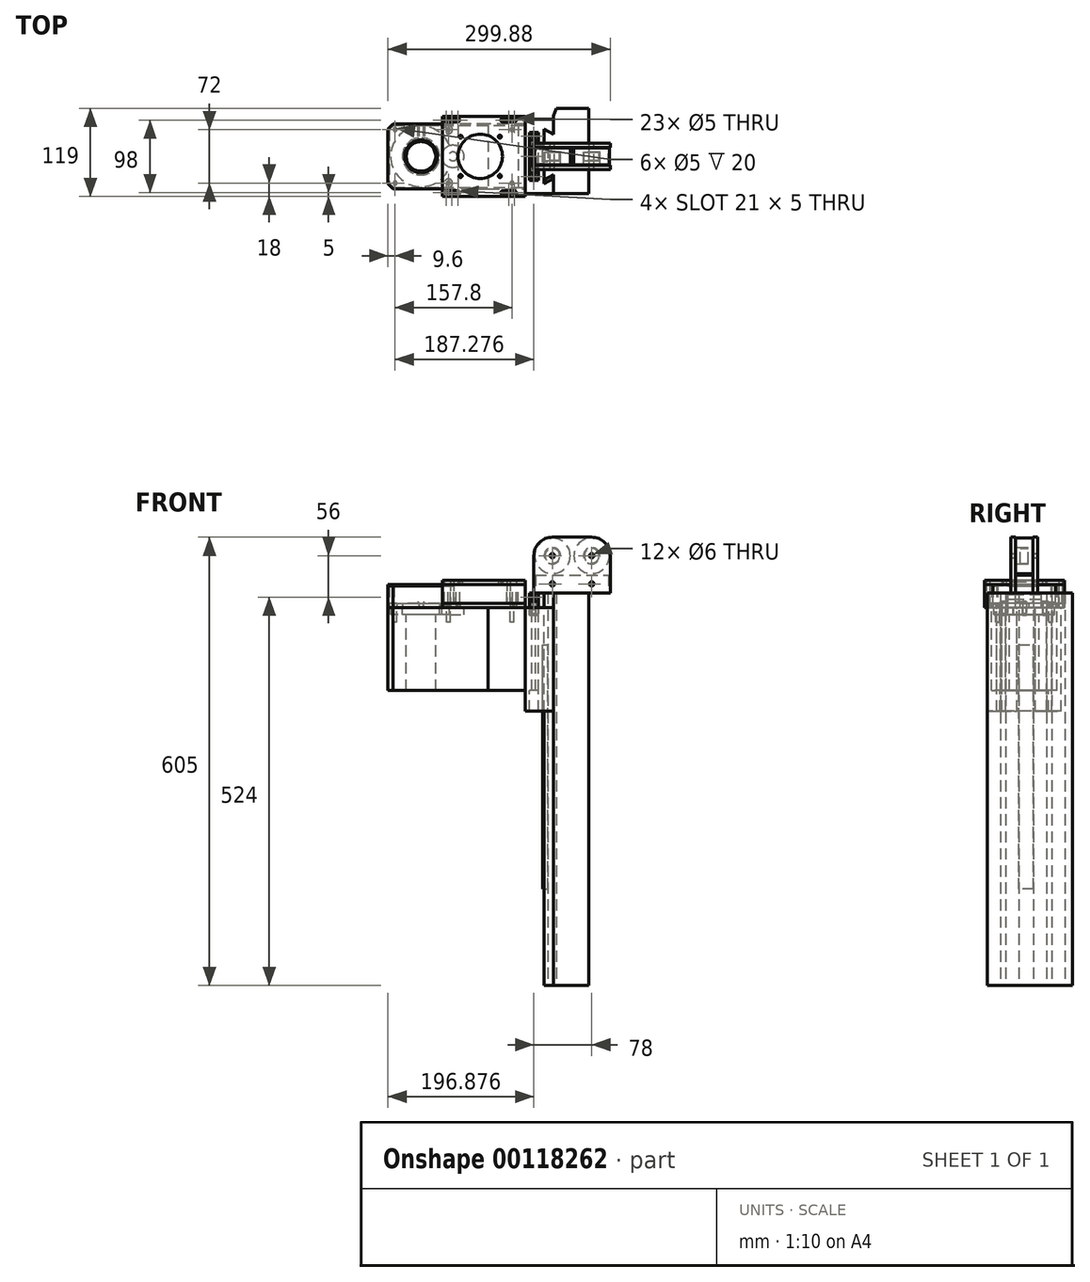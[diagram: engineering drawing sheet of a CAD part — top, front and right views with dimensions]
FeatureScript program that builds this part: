
annotation { "Feature Type Name" : "Feature", "Feature Type Description" : "" }
export const myFeature = defineFeature(function(context is Context, id is Id, definition is map)
    precondition{}
    {
        {
            var Q0;
            Q0=qCreatedBy(makeId("Top.planeOp"),FACE);
            cPlane(context, id + "F0", {"entities" : qUnion([Q0]), "cplaneType" : CPlaneType.OFFSET, "offset" : 31 * mm, "width" : 150 * mm, "height" : 150 * mm});
        }
        {
            var Q0;
            Q0=qCreatedBy(makeId("Top.planeOp"),FACE);
            var sketch = newSketch(context, id + "F1", { "sketchPlane" : qUnion([Q0])});
            skLineSegment(sketch, "E0", {"start": v(0, 0) * mm, "end": v(-38, 0) * mm});
            skLineSegment(sketch, "E1", {"start": v(-38, 0) * mm, "end": v(-38, -6) * mm});
            skLineSegment(sketch, "E2", {"start": v(-38, -6) * mm, "end": v(-88, -6) * mm});
            skLineSegment(sketch, "E3", {"start": v(-88, -6) * mm, "end": v(-88, -94) * mm});
            skLineSegment(sketch, "E4", {"start": v(-88, -94) * mm, "end": v(-38, -94) * mm});
            skLineSegment(sketch, "E5", {"start": v(-38, -94) * mm, "end": v(-38, -100) * mm});
            skLineSegment(sketch, "E6", {"start": v(-38, -100) * mm, "end": v(0, -100) * mm});
            skLineSegment(sketch, "E7", {"start": v(0, -100) * mm, "end": v(0, -80) * mm});
            skLineSegment(sketch, "E8", {"start": v(0, -80) * mm, "end": v(-12.12, -87) * mm});
            skLineSegment(sketch, "E9", {"start": v(-12.12, -87) * mm, "end": v(-12.12, -60) * mm});
            skLineSegment(sketch, "E10", {"start": v(-12.12, -60) * mm, "end": v(-20.12, -60) * mm});
            skLineSegment(sketch, "E11", {"start": v(-20.12, -60) * mm, "end": v(-20.12, -35) * mm});
            skLineSegment(sketch, "E12", {"start": v(-20.12, -35) * mm, "end": v(-12.12, -35) * mm});
            skLineSegment(sketch, "E13", {"start": v(-12.12, -35) * mm, "end": v(-12.12, -13) * mm});
            skLineSegment(sketch, "E14", {"start": v(-12.12, -13) * mm, "end": v(0, -20) * mm});
            skLineSegment(sketch, "E15", {"start": v(0, -20) * mm, "end": v(0, 0) * mm});
            skLineSegment(sketch, "E16", {"start": v(-88, -6) * mm, "end": v(-215.93, -6) * mm});
            skLineSegment(sketch, "E17", {"start": v(-223, -13.07) * mm, "end": v(-223, -86.93) * mm});
            skLineSegment(sketch, "E18", {"start": v(-215.93, -94) * mm, "end": v(-88, -94) * mm});
            skLineSegment(sketch, "E19", {"start": v(-215.93, -6) * mm, "end": v(-223, -13.07) * mm});
            skLineSegment(sketch, "E20", {"start": v(-215.93, -94) * mm, "end": v(-223, -86.93) * mm});
            skCircle(sketch, "E21", {"center": v(-213.4, -86) * mm, "radius": 2.5 * mm});
            skCircle(sketch, "E22.0.1.0", {"center": v(-213.4, -14) * mm, "radius": 2.5 * mm});
            skCircle(sketch, "E22.1.0.0", {"center": v(-141.4, -86) * mm, "radius": 2.5 * mm});
            skCircle(sketch, "E22.1.1.0", {"center": v(-141.4, -14) * mm, "radius": 2.5 * mm});
            skLineSegment(sketch, "E22.direction1", {"start": v(-213.4, -86) * mm, "end": v(-141.4, -86) * mm, "construction": true});
            skLineSegment(sketch, "E22.direction2", {"start": v(-213.4, -86) * mm, "end": v(-213.4, -14) * mm, "construction": true});
            skCircle(sketch, "E23.1.0.0", {"center": v(-55.6, -14) * mm, "radius": 2.5 * mm});
            skCircle(sketch, "E23.1.1.0", {"center": v(-55.6, -86) * mm, "radius": 2.5 * mm});
            skLineSegment(sketch, "E23.direction1", {"start": v(-141.4, -14) * mm, "end": v(-55.6, -14) * mm, "construction": true});
            skLineSegment(sketch, "E23.direction2", {"start": v(-141.4, -14) * mm, "end": v(-141.4, -86) * mm, "construction": true});
            skLineSegment(sketch, "E24", {"start": v(-55.6, -14) * mm, "end": v(-55.6, -86) * mm, "construction": true});
            skLineSegment(sketch, "E25", {"start": v(-55.6, -86) * mm, "end": v(-141.4, -86) * mm, "construction": true});
            skLineSegment(sketch, "E26", {"start": v(-98.5, -14) * mm, "end": v(-98.5, -86) * mm, "construction": true});
            skPoint(sketch, "E27", {"position": v(-98.5, -50) * mm});
            skLineSegment(sketch, "E28", {"start": v(-223, -50) * mm, "end": v(-98.5, -50) * mm, "construction": true});
            skCircle(sketch, "E29", {"center": v(-178.5, -50) * mm, "radius": 25 * mm});
            skCircle(sketch, "E30", {"center": v(-135.42, -50) * mm, "radius": 15 * mm});
            skCircle(sketch, "E31", {"center": v(-178.5, -50) * mm, "radius": 14 * mm});
            skCircle(sketch, "E32", {"center": v(-178.5, -50) * mm, "radius": 20 * mm});
            skCircle(sketch, "E33", {"center": v(-178.5, -50) * mm, "radius": 41 * mm});
            skLineSegment(sketch, "E34", {"start": v(-38, -6) * mm, "end": v(-38, -94) * mm});
            skLineSegment(sketch, "E35", {"start": v(-20.12, -17.5) * mm, "end": v(-32.12, -17.5) * mm});
            skLineSegment(sketch, "E36", {"start": v(-20.12, -17.5) * mm, "end": v(-20.12, -35) * mm});
            skLineSegment(sketch, "E37", {"start": v(-32.12, -17.5) * mm, "end": v(-32.12, -82.5) * mm});
            skLineSegment(sketch, "E38", {"start": v(-32.12, -27.5) * mm, "end": v(-20.12, -27.5) * mm});
            skLineSegment(sketch, "E39.MirrorCS", {"start": v(-32.12, -72.5) * mm, "end": v(-20.12, -72.5) * mm});
            skLineSegment(sketch, "E40.MirrorCS", {"start": v(-20.12, -82.5) * mm, "end": v(-32.12, -82.5) * mm});
            skLineSegment(sketch, "E41", {"start": v(-20.12, -82.5) * mm, "end": v(-20.12, -60) * mm});
            skLineSegment(sketch, "E42", {"start": v(-32.12, -37.5) * mm, "end": v(-20.12, -37.5) * mm});
            skLineSegment(sketch, "E43.MirrorCS", {"start": v(-32.12, -62.5) * mm, "end": v(-20.12, -62.5) * mm});
            skLineSegment(sketch, "E44", {"start": v(-32.12, -27.5) * mm, "end": v(-20.12, -17.5) * mm, "construction": true});
            skLineSegment(sketch, "E45", {"start": v(-20.12, -27.5) * mm, "end": v(-32.12, -17.5) * mm, "construction": true});
            skCircle(sketch, "E46", {"center": v(-26.12, -22.5) * mm, "radius": 2.5 * mm});
            skCircle(sketch, "E47.MirrorC", {"center": v(-26.12, -77.5) * mm, "radius": 2.5 * mm});
            skCircle(sketch, "E48", {"center": v(-26.12, -50) * mm, "radius": 2.5 * mm});
            skPoint(sketch, "E48.centerSnap0", {"position": v(-26.12, -62.5) * mm});
            skPoint(sketch, "E48.centerSnap1", {"position": v(-32.12, -50) * mm});
            skSolve(sketch);
        }
        {
            var Q0;
            Q0=qCreatedBy(makeId("Top.planeOp"),FACE);
            var sketch = newSketch(context, id + "F2", { "sketchPlane" : qUnion([Q0])});
            skLineSegment(sketch, "E49.0", {"start": v(-88, -6) * mm, "end": v(-149.4, -6) * mm});
            skLineSegment(sketch, "E49.4", {"start": v(-149.4, -94) * mm, "end": v(-88, -94) * mm});
            skLineSegment(sketch, "E49.5", {"start": v(-47.6, -6) * mm, "end": v(-88, -6) * mm});
            skLineSegment(sketch, "E49.6", {"start": v(-88, -94) * mm, "end": v(-47.6, -94) * mm});
            skCircle(sketch, "E49.7", {"center": v(-55.6, -86) * mm, "radius": 2.5 * mm});
            skCircle(sketch, "E49.8", {"center": v(-55.6, -14) * mm, "radius": 2.5 * mm});
            skCircle(sketch, "E49.9", {"center": v(-141.4, -14) * mm, "radius": 2.5 * mm});
            skCircle(sketch, "E49.10", {"center": v(-141.4, -86) * mm, "radius": 2.5 * mm});
            skCircle(sketch, "E49.11", {"center": v(-213.4, -86) * mm, "radius": 2.5 * mm});
            skCircle(sketch, "E49.12", {"center": v(-213.4, -14) * mm, "radius": 2.5 * mm});
            skLineSegment(sketch, "E49.13", {"start": v(-98.5, -14) * mm, "end": v(-98.5, -86) * mm, "construction": true});
            skLineSegment(sketch, "E49.14", {"start": v(-141.4, -14) * mm, "end": v(-55.6, -14) * mm, "construction": true});
            skLineSegment(sketch, "E49.15", {"start": v(-55.6, -14) * mm, "end": v(-55.6, -86) * mm, "construction": true});
            skLineSegment(sketch, "E49.16", {"start": v(-55.6, -86) * mm, "end": v(-141.4, -86) * mm, "construction": true});
            skLineSegment(sketch, "E49.17", {"start": v(-141.4, -14) * mm, "end": v(-141.4, -86) * mm, "construction": true});
            skCircle(sketch, "E49.18", {"center": v(-178.5, -50) * mm, "radius": 25 * mm});
            skLineSegment(sketch, "E50", {"start": v(-47.6, -6) * mm, "end": v(-47.6, -94) * mm});
            skLineSegment(sketch, "E51", {"start": v(-149.4, -6) * mm, "end": v(-149.4, -94) * mm, "construction": true});
            skPoint(sketch, "E52", {"position": v(-149.4, -6) * mm});
            skPoint(sketch, "E53", {"position": v(-149.4, -94) * mm});
            skPoint(sketch, "E54.orphan", {"position": v(-215.93, -94) * mm});
            skLineSegment(sketch, "E55.0", {"start": v(-215.1, -8) * mm, "end": v(-149.4, -8) * mm});
            skLineSegment(sketch, "E55.1", {"start": v(-215.1, -92) * mm, "end": v(-149.4, -92) * mm});
            skLineSegment(sketch, "E55.2", {"start": v(-215.1, -92) * mm, "end": v(-221, -86.1) * mm});
            skLineSegment(sketch, "E55.3", {"start": v(-221, -13.9) * mm, "end": v(-221, -86.1) * mm});
            skLineSegment(sketch, "E55.4", {"start": v(-215.1, -8) * mm, "end": v(-221, -13.9) * mm});
            skLineSegment(sketch, "E56.0", {"start": v(-88, 4) * mm, "end": v(-149.4, 4) * mm});
            skLineSegment(sketch, "E56.1", {"start": v(-47.6, 4) * mm, "end": v(-88, 4) * mm});
            skLineSegment(sketch, "E57.0", {"start": v(-88, -104) * mm, "end": v(-47.6, -104) * mm});
            skLineSegment(sketch, "E57.1", {"start": v(-149.4, -104) * mm, "end": v(-88, -104) * mm});
            skLineSegment(sketch, "E58", {"start": v(-149.4, -92) * mm, "end": v(-149.4, -94) * mm});
            skLineSegment(sketch, "E59", {"start": v(-149.4, -104) * mm, "end": v(-149.4, -94) * mm});
            skLineSegment(sketch, "E60", {"start": v(-47.6, -104) * mm, "end": v(-47.6, -94) * mm});
            skLineSegment(sketch, "E61", {"start": v(-149.4, -6) * mm, "end": v(-149.4, 4) * mm});
            skLineSegment(sketch, "E62", {"start": v(-47.6, -6) * mm, "end": v(-47.6, 4) * mm});
            skLineSegment(sketch, "E63", {"start": v(-149.4, -8) * mm, "end": v(-149.4, -6) * mm});
            skPoint(sketch, "E49.2.end.orphan", {"position": v(-223, -86.93) * mm});
            skPoint(sketch, "E49.3.end.orphan", {"position": v(-223, -86.93) * mm});
            skCircle(sketch, "E64", {"center": v(-98.5, -50) * mm, "radius": 25 * mm});
            skLineSegment(sketch, "E65", {"start": v(-178.5, -25) * mm, "end": v(-98.5, -25) * mm});
            skLineSegment(sketch, "E66", {"start": v(-178.5, -75) * mm, "end": v(-98.5, -75) * mm});
            skCircle(sketch, "E67", {"center": v(-98.5, -50) * mm, "radius": 45 * mm, "construction": true});
            skPoint(sketch, "E68.centerSnap0", {"position": v(-149.4, -99) * mm});
            skLineSegment(sketch, "E69", {"start": v(-47.6, 4) * mm, "end": v(-149.4, -104) * mm, "construction": true});
            skLineSegment(sketch, "E70", {"start": v(-149.4, 4) * mm, "end": v(-47.6, -104) * mm, "construction": true});
            skPoint(sketch, "E71.centerSnap0", {"position": v(-47.6, -99) * mm});
            skCircle(sketch, "E72", {"center": v(-144.69, -99) * mm, "radius": 2.5 * mm});
            skCircle(sketch, "E73", {"center": v(-144.69, -1) * mm, "radius": 2.5 * mm});
            skCircle(sketch, "E74", {"center": v(-52.31, -1) * mm, "radius": 2.5 * mm});
            skCircle(sketch, "E75", {"center": v(-52.31, -99) * mm, "radius": 2.5 * mm});
            skCircle(sketch, "E76", {"center": v(-136.69, -1) * mm, "radius": 2.1 * mm});
            skCircle(sketch, "E77", {"center": v(-60.31, -1) * mm, "radius": 2.1 * mm});
            skCircle(sketch, "E78", {"center": v(-136.69, -99) * mm, "radius": 2.1 * mm});
            skCircle(sketch, "E79", {"center": v(-60.31, -99) * mm, "radius": 2.1 * mm});
            skLineSegment(sketch, "E80", {"start": v(-47.6, 4) * mm, "end": v(-38, 4) * mm});
            skLineSegment(sketch, "E81", {"start": v(-38, 4) * mm, "end": v(-38, -104) * mm});
            skLineSegment(sketch, "E82", {"start": v(-38, -104) * mm, "end": v(-47.6, -104) * mm});
            skLineSegment(sketch, "E83.0", {"start": v(-38, -6) * mm, "end": v(-38, -94) * mm});
            skLineSegment(sketch, "E84.0", {"start": v(-215.93, -6) * mm, "end": v(-149.4, -6) * mm});
            skLineSegment(sketch, "E84.1", {"start": v(-215.93, -94) * mm, "end": v(-149.4, -94) * mm});
            skLineSegment(sketch, "E84.2", {"start": v(-215.93, -94) * mm, "end": v(-223, -86.93) * mm});
            skLineSegment(sketch, "E84.3", {"start": v(-223, -13.07) * mm, "end": v(-223, -86.93) * mm});
            skLineSegment(sketch, "E84.4", {"start": v(-215.93, -6) * mm, "end": v(-223, -13.07) * mm});
            skLineSegment(sketch, "E85", {"start": v(-178.5, -25) * mm, "end": v(-178.5, -8) * mm, "construction": true});
            skLineSegment(sketch, "E86", {"start": v(-181.5, -8) * mm, "end": v(-181.5, -25.18) * mm});
            skLineSegment(sketch, "E87.MirrorCS", {"start": v(-175.5, -8) * mm, "end": v(-175.5, -25.18) * mm});
            skLineSegment(sketch, "E88", {"start": v(-136.69, -1) * mm, "end": v(-136.69, -99) * mm, "construction": true});
            skCircle(sketch, "E89.MirrorC", {"center": v(-128.69, -99) * mm, "radius": 2.5 * mm});
            skCircle(sketch, "E90.MirrorC", {"center": v(-128.69, -1) * mm, "radius": 2.5 * mm});
            skCircle(sketch, "E91.0", {"center": v(-135.42, -50) * mm, "radius": 15 * mm});
            skCircle(sketch, "E92", {"center": v(-135.42, -50) * mm, "radius": 6 * mm});
            skSolve(sketch);
        }
        {
            var Q0;
            Q0=qCreatedBy(id+"F0.planeOp",FACE);
            var sketch = newSketch(context, id + "F3", { "sketchPlane" : qUnion([Q0])});
            skLineSegment(sketch, "E93.0", {"start": v(-88, 4) * mm, "end": v(-149.4, 4) * mm});
            skLineSegment(sketch, "E93.1", {"start": v(-47.6, 4) * mm, "end": v(-88, 4) * mm});
            skLineSegment(sketch, "E93.2", {"start": v(-47.6, -6) * mm, "end": v(-47.6, 4) * mm});
            skLineSegment(sketch, "E93.3", {"start": v(-47.6, -6) * mm, "end": v(-47.6, -94) * mm});
            skLineSegment(sketch, "E93.4", {"start": v(-47.6, -104) * mm, "end": v(-47.6, -94) * mm});
            skLineSegment(sketch, "E93.5", {"start": v(-88, -104) * mm, "end": v(-47.6, -104) * mm});
            skLineSegment(sketch, "E93.6", {"start": v(-149.4, -104) * mm, "end": v(-88, -104) * mm});
            skLineSegment(sketch, "E93.7", {"start": v(-149.4, -104) * mm, "end": v(-149.4, -94) * mm});
            skLineSegment(sketch, "E93.8", {"start": v(-149.4, -6) * mm, "end": v(-149.4, -94) * mm});
            skLineSegment(sketch, "E93.9", {"start": v(-149.4, -6) * mm, "end": v(-149.4, 4) * mm});
            skCircle(sketch, "E93.10", {"center": v(-52.31, -1) * mm, "radius": 2.5 * mm});
            skCircle(sketch, "E93.11", {"center": v(-144.69, -1) * mm, "radius": 2.5 * mm});
            skCircle(sketch, "E93.12", {"center": v(-136.69, -1) * mm, "radius": 2.1 * mm});
            skCircle(sketch, "E93.13", {"center": v(-60.31, -1) * mm, "radius": 2.1 * mm});
            skCircle(sketch, "E93.14", {"center": v(-52.31, -99) * mm, "radius": 2.5 * mm});
            skCircle(sketch, "E93.15", {"center": v(-60.31, -99) * mm, "radius": 2.1 * mm});
            skCircle(sketch, "E93.16", {"center": v(-136.69, -99) * mm, "radius": 2.1 * mm});
            skCircle(sketch, "E93.17", {"center": v(-144.69, -99) * mm, "radius": 2.5 * mm});
            skCircle(sketch, "E94.0", {"center": v(-98.5, -50) * mm, "radius": 45 * mm, "construction": true});
            skCircle(sketch, "E95", {"center": v(-98.5, -50) * mm, "radius": 30 * mm});
            skLineSegment(sketch, "E96", {"start": v(-144.69, -1) * mm, "end": v(-52.31, -1) * mm, "construction": true});
            skLineSegment(sketch, "E97", {"start": v(-52.31, -99) * mm, "end": v(-144.69, -99) * mm, "construction": true});
            skCircle(sketch, "E98", {"center": v(-128.69, -1) * mm, "radius": 2.5 * mm});
            skCircle(sketch, "E99", {"center": v(-68.31, -1) * mm, "radius": 2.5 * mm});
            skCircle(sketch, "E100", {"center": v(-68.31, -99) * mm, "radius": 2.5 * mm});
            skCircle(sketch, "E101", {"center": v(-128.69, -99) * mm, "radius": 2.5 * mm});
            skLineSegment(sketch, "E102", {"start": v(-144.69, 1.5) * mm, "end": v(-128.69, 1.5) * mm});
            skLineSegment(sketch, "E103", {"start": v(-144.69, -3.5) * mm, "end": v(-128.69, -3.5) * mm});
            skCircle(sketch, "E104", {"center": v(-98.5, -50) * mm, "radius": 37.5 * mm, "construction": true});
            skCircle(sketch, "E105", {"center": v(-125.02, -23.48) * mm, "radius": 2.1 * mm});
            skCircle(sketch, "E106", {"center": v(-125.02, -76.52) * mm, "radius": 2.1 * mm});
            skCircle(sketch, "E107", {"center": v(-71.98, -76.52) * mm, "radius": 2.1 * mm});
            skCircle(sketch, "E108", {"center": v(-71.98, -23.48) * mm, "radius": 2.1 * mm});
            skLineSegment(sketch, "E109.MirrorCS", {"start": v(-52.31, -3.5) * mm, "end": v(-68.31, -3.5) * mm});
            skLineSegment(sketch, "E110.MirrorCS", {"start": v(-52.31, 1.5) * mm, "end": v(-68.31, 1.5) * mm});
            skLineSegment(sketch, "E111.MirrorCS", {"start": v(-144.69, -96.5) * mm, "end": v(-128.69, -96.5) * mm});
            skLineSegment(sketch, "E112.MirrorCS", {"start": v(-144.69, -101.5) * mm, "end": v(-128.69, -101.5) * mm});
            skLineSegment(sketch, "E113.MirrorCS", {"start": v(-52.31, -96.5) * mm, "end": v(-68.31, -96.5) * mm});
            skLineSegment(sketch, "E114.MirrorCS", {"start": v(-52.31, -101.5) * mm, "end": v(-68.31, -101.5) * mm});
            skLineSegment(sketch, "E115", {"start": v(-149.4, -6) * mm, "end": v(-47.6, -6) * mm});
            skLineSegment(sketch, "E116", {"start": v(-149.4, -94) * mm, "end": v(-47.6, -94) * mm});
            skLineSegment(sketch, "E117.0", {"start": v(-38, -6) * mm, "end": v(-38, -94) * mm});
            skLineSegment(sketch, "E118", {"start": v(-47.6, 4) * mm, "end": v(-38, 4) * mm});
            skLineSegment(sketch, "E119", {"start": v(-38, 4) * mm, "end": v(-38, -104) * mm});
            skLineSegment(sketch, "E120", {"start": v(-38, -104) * mm, "end": v(-47.6, -104) * mm});
            skLineSegment(sketch, "E121", {"start": v(-47.6, -6) * mm, "end": v(-38, -6) * mm});
            skLineSegment(sketch, "E122", {"start": v(-47.6, -94) * mm, "end": v(-38, -94) * mm});
            skLineSegment(sketch, "E123", {"start": v(-98.5, -120.58) * mm, "end": v(-98.5, 19.86) * mm, "construction": true});
            skPoint(sketch, "E123.endSnap0", {"position": v(-98.5, -1) * mm});
            skLineSegment(sketch, "E124", {"start": v(-98.5, -50) * mm, "end": v(-71.98, -23.48) * mm, "construction": true});
            skLineSegment(sketch, "E125", {"start": v(-98.5, -50) * mm, "end": v(-125.02, -23.48) * mm, "construction": true});
            skLineSegment(sketch, "E126", {"start": v(-98.5, -50) * mm, "end": v(-125.02, -76.52) * mm, "construction": true});
            skLineSegment(sketch, "E127", {"start": v(-98.5, -50) * mm, "end": v(-71.98, -76.52) * mm, "construction": true});
            skLineSegment(sketch, "E128", {"start": v(-149.4, -92) * mm, "end": v(-47.6, -92) * mm});
            skLineSegment(sketch, "E129", {"start": v(-149.4, -50) * mm, "end": v(-47.6, -50) * mm, "construction": true});
            skLineSegment(sketch, "E130.MirrorCS", {"start": v(-149.4, -8) * mm, "end": v(-47.6, -8) * mm});
            skLineSegment(sketch, "E131", {"start": v(-47.6, -92) * mm, "end": v(-38, -92) * mm});
            skLineSegment(sketch, "E132.MirrorCS", {"start": v(-47.6, -8) * mm, "end": v(-38, -8) * mm});
            skSolve(sketch);
        }
        {
            var Q0;
            Q0=makeQuery(id+"F1.imprint","IMPRINT",FACE,{"disambiguationData":[TD([[makeQuery(id+"F1.imprint","IMPRINT",EDGE,{"derivedFrom":sQuery(id+"F1.wireOp",EDGE,"E0")}),1.0]])]});
            extrude(context, id + "F4", {"entities" : qUnion([Q0]), "oppositeDirection" : true, "depth" : 140 * mm});
        }
        {
            var Q0;
            Q0=makeQuery(id+"F1.imprint","IMPRINT",FACE,{"disambiguationData":[TD([[makeQuery(id+"F1.imprint","IMPRINT",EDGE,{"derivedFrom":sQuery(id+"F1.wireOp",EDGE,"E2")}),1.0]])]});
            var Q1;
            Q1=makeQuery(id+"F1.imprint","IMPRINT",FACE,{"disambiguationData":[TD([[makeQuery(id+"F1.imprint","IMPRINT",EDGE,{"derivedFrom":sQuery(id+"F1.wireOp",EDGE,"E23.1.1.0")}),1.0]])]});
            var Q2;
            Q2=makeQuery(id+"F1.imprint","IMPRINT",FACE,{"disambiguationData":[TD([[makeQuery(id+"F1.imprint","IMPRINT",EDGE,{"derivedFrom":sQuery(id+"F1.wireOp",EDGE,"E23.1.0.0")}),1.0]])]});
            var Q3;
            Q3=makeQuery(id+"F1.imprint","IMPRINT",FACE,{"disambiguationData":[TD([[makeQuery(id+"F1.imprint","IMPRINT",EDGE,{"derivedFrom":sQuery(id+"F1.wireOp",EDGE,"E47.MirrorC")}),-1.0]])]});
            var Q4;
            {var subQ1=sQuery(id+"F1.wireOp",EDGE,"E39.MirrorCS");Q4=makeQuery(id+"F1.imprint","IMPRINT",FACE,{"disambiguationData":[TD([[makeQuery(id+"F1.imprint","IMPRINT",EDGE,{"derivedFrom":subQ1}),-1.0]])]});}
            var Q5;
            {var subQ0=sQuery(id+"F1.wireOp",EDGE,"E39.MirrorCS");Q5=makeQuery(id+"F1.imprint","IMPRINT",FACE,{"disambiguationData":[TD([[makeQuery(id+"F1.imprint","IMPRINT",EDGE,{"derivedFrom":subQ0}),1.0]])]});}
            var Q6;
            {var subQ4=sQuery(id+"F1.wireOp",EDGE,"E42");Q6=makeQuery(id+"F1.imprint","IMPRINT",FACE,{"disambiguationData":[TD([[makeQuery(id+"F1.imprint","IMPRINT",EDGE,{"derivedFrom":subQ4}),-1.0]])]});}
            var Q7;
            Q7=makeQuery(id+"F1.imprint","IMPRINT",FACE,{"disambiguationData":[TD([[makeQuery(id+"F1.imprint","IMPRINT",EDGE,{"derivedFrom":sQuery(id+"F1.wireOp",EDGE,"E48")}),1.0]])]});
            var Q8;
            {var subQ0=sQuery(id+"F1.wireOp",EDGE,"E38");Q8=makeQuery(id+"F1.imprint","IMPRINT",FACE,{"disambiguationData":[TD([[makeQuery(id+"F1.imprint","IMPRINT",EDGE,{"derivedFrom":subQ0}),-1.0]])]});}
            var Q9;
            {var subQ2=sQuery(id+"F1.wireOp",EDGE,"E35");Q9=makeQuery(id+"F1.imprint","IMPRINT",FACE,{"disambiguationData":[TD([[makeQuery(id+"F1.imprint","IMPRINT",EDGE,{"derivedFrom":subQ2}),1.0]])]});}
            var Q10;
            Q10=makeQuery(id+"F1.imprint","IMPRINT",FACE,{"disambiguationData":[TD([[makeQuery(id+"F1.imprint","IMPRINT",EDGE,{"derivedFrom":sQuery(id+"F1.wireOp",EDGE,"E46")}),1.0]])]});
            extrude(context, id + "F5", {"entities" : qUnion([Q0, Q1, Q2, Q3, Q4, Q5, Q6, Q7, Q8, Q9, Q10]), "operationType" : NewBodyOperationType.ADD, "oppositeDirection" : true, "depth" : 112 * mm});
        }
        {
            var Q0;
            Q0=makeQuery(id+"F1.imprint","IMPRINT",FACE,{"disambiguationData":[TD([[makeQuery(id+"F1.imprint","IMPRINT",EDGE,{"derivedFrom":sQuery(id+"F1.wireOp",EDGE,"E3")}),-1.0]])]});
            var Q1;
            Q1=makeQuery(id+"F1.imprint","IMPRINT",FACE,{"disambiguationData":[TD([[makeQuery(id+"F1.imprint","IMPRINT",EDGE,{"derivedFrom":sQuery(id+"F1.wireOp",EDGE,"E29")}),-1.0]])]});
            var Q2;
            {var subQ0=sQuery(id+"F1.wireOp",EDGE,"E33");var subQ1=sQuery(id+"F1.wireOp",EDGE,"E30");var subQ2=makeQuery(id+"F1.imprint","INTERSECT",VERTEX,{"disambiguationData":[OD(0.0)],"derivedFrom":[subQ1,subQ0]});Q2=makeQuery(id+"F1.imprint","IMPRINT",FACE,{"disambiguationData":[TD([[makeQuery(id+"F1.imprint","IMPRINT",EDGE,{"disambiguationData":[TD([[subQ2,-1.0]])],"derivedFrom":subQ1}),1.0]])]});}
            var Q3;
            Q3=makeQuery(id+"F1.imprint","IMPRINT",FACE,{"disambiguationData":[TD([[makeQuery(id+"F1.imprint","IMPRINT",EDGE,{"derivedFrom":sQuery(id+"F1.wireOp",EDGE,"E29")}),1.0]])]});
            var Q4;
            {var subQ0=sQuery(id+"F1.wireOp",EDGE,"E33");var subQ1=sQuery(id+"F1.wireOp",EDGE,"E30");var subQ2=makeQuery(id+"F1.imprint","INTERSECT",VERTEX,{"disambiguationData":[OD(0.0)],"derivedFrom":[subQ1,subQ0]});Q4=makeQuery(id+"F1.imprint","IMPRINT",FACE,{"disambiguationData":[TD([[makeQuery(id+"F1.imprint","IMPRINT",EDGE,{"disambiguationData":[TD([[subQ2,1.0]])],"derivedFrom":subQ1}),1.0]])]});}
            var Q5;
            Q5=makeQuery(id+"F1.imprint","IMPRINT",FACE,{"disambiguationData":[TD([[makeQuery(id+"F1.imprint","IMPRINT",EDGE,{"derivedFrom":sQuery(id+"F1.wireOp",EDGE,"E22.1.0.0")}),1.0]])]});
            var Q6;
            Q6=makeQuery(id+"F1.imprint","IMPRINT",FACE,{"disambiguationData":[TD([[makeQuery(id+"F1.imprint","IMPRINT",EDGE,{"derivedFrom":sQuery(id+"F1.wireOp",EDGE,"E22.1.1.0")}),1.0]])]});
            var Q7;
            Q7=makeQuery(id+"F1.imprint","IMPRINT",FACE,{"disambiguationData":[TD([[makeQuery(id+"F1.imprint","IMPRINT",EDGE,{"derivedFrom":sQuery(id+"F1.wireOp",EDGE,"E22.0.1.0")}),1.0]])]});
            var Q8;
            Q8=makeQuery(id+"F1.imprint","IMPRINT",FACE,{"disambiguationData":[TD([[makeQuery(id+"F1.imprint","IMPRINT",EDGE,{"derivedFrom":sQuery(id+"F1.wireOp",EDGE,"E21")}),1.0]])]});
            extrude(context, id + "F6", {"entities" : qUnion([Q0, Q1, Q2, Q3, Q4, Q5, Q6, Q7, Q8]), "oppositeDirection" : true, "depth" : 112 * mm});
        }
        {
            var Q0;
            Q0=makeQuery(id+"F1.imprint","IMPRINT",FACE,{"disambiguationData":[TD([[makeQuery(id+"F1.imprint","IMPRINT",EDGE,{"derivedFrom":sQuery(id+"F1.wireOp",EDGE,"E29")}),-1.0]])]});
            var Q1;
            {var subQ0=sQuery(id+"F1.wireOp",EDGE,"E33");var subQ1=sQuery(id+"F1.wireOp",EDGE,"E30");var subQ2=makeQuery(id+"F1.imprint","INTERSECT",VERTEX,{"disambiguationData":[OD(0.0)],"derivedFrom":[subQ1,subQ0]});Q1=makeQuery(id+"F1.imprint","IMPRINT",FACE,{"disambiguationData":[TD([[makeQuery(id+"F1.imprint","IMPRINT",EDGE,{"disambiguationData":[TD([[subQ2,-1.0]])],"derivedFrom":subQ1}),1.0]])]});}
            var Q2;
            {var subQ0=sQuery(id+"F1.wireOp",EDGE,"E33");var subQ1=sQuery(id+"F1.wireOp",EDGE,"E30");var subQ2=makeQuery(id+"F1.imprint","INTERSECT",VERTEX,{"disambiguationData":[OD(0.0)],"derivedFrom":[subQ1,subQ0]});Q2=makeQuery(id+"F1.imprint","IMPRINT",FACE,{"disambiguationData":[TD([[makeQuery(id+"F1.imprint","IMPRINT",EDGE,{"disambiguationData":[TD([[subQ2,1.0]])],"derivedFrom":subQ1}),1.0]])]});}
            var Q3;
            Q3=makeQuery(id+"F1.imprint","IMPRINT",FACE,{"disambiguationData":[TD([[makeQuery(id+"F1.imprint","IMPRINT",EDGE,{"derivedFrom":sQuery(id+"F1.wireOp",EDGE,"E29")}),1.0]])]});
            extrude(context, id + "F7", {"entities" : qUnion([Q0, Q1, Q2, Q3]), "operationType" : NewBodyOperationType.REMOVE, "oppositeDirection" : true, "depth" : 9.5 * mm});
        }
        {
            var Q0;
            Q0=makeQuery(id+"F1.imprint","IMPRINT",FACE,{"disambiguationData":[TD([[makeQuery(id+"F1.imprint","IMPRINT",EDGE,{"derivedFrom":sQuery(id+"F1.wireOp",EDGE,"E29")}),-1.0]])]});
            extrude(context, id + "F8", {"entities" : qUnion([Q0]), "endBound" : BoundingType.UP_TO_NEXT, "oppositeDirection" : true, "depth" : (9) * mm});
        }
        {
            var Q0;
            Q0=makeQuery(id+"F1.imprint","IMPRINT",FACE,{"disambiguationData":[TD([[makeQuery(id+"F1.imprint","IMPRINT",EDGE,{"derivedFrom":sQuery(id+"F1.wireOp",EDGE,"E22.0.1.0")}),1.0]])]});
            var Q1;
            Q1=makeQuery(id+"F1.imprint","IMPRINT",FACE,{"disambiguationData":[TD([[makeQuery(id+"F1.imprint","IMPRINT",EDGE,{"derivedFrom":sQuery(id+"F1.wireOp",EDGE,"E23.1.0.0")}),1.0]])]});
            var Q2;
            Q2=makeQuery(id+"F1.imprint","IMPRINT",FACE,{"disambiguationData":[TD([[makeQuery(id+"F1.imprint","IMPRINT",EDGE,{"derivedFrom":sQuery(id+"F1.wireOp",EDGE,"E23.1.1.0")}),1.0]])]});
            var Q3;
            Q3=makeQuery(id+"F1.imprint","IMPRINT",FACE,{"disambiguationData":[TD([[makeQuery(id+"F1.imprint","IMPRINT",EDGE,{"derivedFrom":sQuery(id+"F1.wireOp",EDGE,"E21")}),1.0]])]});
            var Q4;
            Q4=makeQuery(id+"F1.imprint","IMPRINT",FACE,{"disambiguationData":[TD([[makeQuery(id+"F1.imprint","IMPRINT",EDGE,{"derivedFrom":sQuery(id+"F1.wireOp",EDGE,"E22.1.0.0")}),1.0]])]});
            var Q5;
            Q5=makeQuery(id+"F1.imprint","IMPRINT",FACE,{"disambiguationData":[TD([[makeQuery(id+"F1.imprint","IMPRINT",EDGE,{"derivedFrom":sQuery(id+"F1.wireOp",EDGE,"E22.1.1.0")}),1.0]])]});
            extrude(context, id + "F9", {"entities" : qUnion([Q0, Q1, Q2, Q3, Q4, Q5]), "operationType" : NewBodyOperationType.REMOVE, "oppositeDirection" : true, "depth" : 20 * mm});
        }
        {
            var Q0;
            {var subQ0=sQuery(id+"F2.wireOp",EDGE,"E65");var subQ1=sQuery(id+"F2.wireOp",EDGE,"E49.18");var subQ2=makeQuery(id+"F2.imprint","INTERSECT",VERTEX,{"derivedFrom":[subQ1,subQ0]});Q0=makeQuery(id+"F2.imprint","IMPRINT",FACE,{"disambiguationData":[TD([[makeQuery(id+"F2.imprint","IMPRINT",EDGE,{"disambiguationData":[TD([[subQ2,-1.0]])],"derivedFrom":subQ1}),-1.0]])]});}
            var Q1;
            {var subQ11=sQuery(id+"F2.wireOp",EDGE,"E49.0");Q1=makeQuery(id+"F2.imprint","IMPRINT",FACE,{"disambiguationData":[TD([[makeQuery(id+"F2.imprint","IMPRINT",EDGE,{"derivedFrom":subQ11}),1.0]])]});}
            var Q2;
            {var subQ1=sQuery(id+"F2.wireOp",EDGE,"E49.5");Q2=makeQuery(id+"F2.imprint","IMPRINT",FACE,{"disambiguationData":[TD([[makeQuery(id+"F2.imprint","IMPRINT",EDGE,{"derivedFrom":subQ1}),1.0]])]});}
            var Q3;
            Q3=makeQuery(id+"F2.imprint","IMPRINT",FACE,{"disambiguationData":[TD([[makeQuery(id+"F2.imprint","IMPRINT",EDGE,{"derivedFrom":sQuery(id+"F2.wireOp",EDGE,"E49.0")}),-1.0]])]});
            var Q4;
            Q4=makeQuery(id+"F2.imprint","IMPRINT",FACE,{"disambiguationData":[TD([[makeQuery(id+"F2.imprint","IMPRINT",EDGE,{"derivedFrom":sQuery(id+"F2.wireOp",EDGE,"E49.4")}),-1.0]])]});
            var Q5;
            Q5=makeQuery(id+"F2.imprint","IMPRINT",FACE,{"disambiguationData":[TD([[makeQuery(id+"F2.imprint","IMPRINT",EDGE,{"derivedFrom":sQuery(id+"F2.wireOp",EDGE,"E77")}),1.0]])]});
            var Q6;
            Q6=makeQuery(id+"F2.imprint","IMPRINT",FACE,{"disambiguationData":[TD([[makeQuery(id+"F2.imprint","IMPRINT",EDGE,{"derivedFrom":sQuery(id+"F2.wireOp",EDGE,"E79")}),1.0]])]});
            var Q7;
            Q7=makeQuery(id+"F2.imprint","IMPRINT",FACE,{"disambiguationData":[TD([[makeQuery(id+"F2.imprint","IMPRINT",EDGE,{"derivedFrom":sQuery(id+"F2.wireOp",EDGE,"E76")}),1.0]])]});
            var Q8;
            Q8=makeQuery(id+"F2.imprint","IMPRINT",FACE,{"disambiguationData":[TD([[makeQuery(id+"F2.imprint","IMPRINT",EDGE,{"derivedFrom":sQuery(id+"F2.wireOp",EDGE,"E78")}),1.0]])]});
            var Q9;
            Q9=makeQuery(id+"F2.imprint","IMPRINT",FACE,{"disambiguationData":[TD([[makeQuery(id+"F2.imprint","IMPRINT",EDGE,{"derivedFrom":sQuery(id+"F2.wireOp",EDGE,"E50")}),1.0]])]});
            var Q10;
            {var subQ0=sQuery(id+"F2.wireOp",EDGE,"E64");var subQ1=makeQuery(id+"F2.imprint","INTERSECT",VERTEX,{"derivedFrom":[subQ0,sQuery(id+"F2.wireOp",EDGE,"E65")]});Q10=makeQuery(id+"F2.imprint","IMPRINT",FACE,{"disambiguationData":[TD([[makeQuery(id+"F2.imprint","IMPRINT",EDGE,{"disambiguationData":[TD([[subQ1,-1.0]])],"derivedFrom":subQ0}),1.0]])]});}
            var Q11;
            {var subQ9=sQuery(id+"F2.wireOp",EDGE,"E66");Q11=makeQuery(id+"F2.imprint","IMPRINT",FACE,{"disambiguationData":[TD([[makeQuery(id+"F2.imprint","IMPRINT",EDGE,{"derivedFrom":subQ9}),1.0]])]});}
            var Q12;
            Q12=makeQuery(id+"F2.imprint","IMPRINT",FACE,{"disambiguationData":[TD([[makeQuery(id+"F2.imprint","IMPRINT",EDGE,{"derivedFrom":sQuery(id+"F2.wireOp",EDGE,"E92")}),-1.0]])]});
            var Q13;
            {var subQ0=sQuery(id+"F2.wireOp",EDGE,"E91.0");var subQ1=sQuery(id+"F2.wireOp",EDGE,"E64");var subQ2=makeQuery(id+"F2.imprint","INTERSECT",VERTEX,{"disambiguationData":[OD(0.0)],"derivedFrom":[subQ1,subQ0]});Q13=makeQuery(id+"F2.imprint","IMPRINT",FACE,{"disambiguationData":[TD([[makeQuery(id+"F2.imprint","IMPRINT",EDGE,{"disambiguationData":[TD([[subQ2,-1.0]])],"derivedFrom":subQ1}),1.0]])]});}
            extrude(context, id + "F10", {"entities" : qUnion([Q0, Q1, Q2, Q3, Q4, Q5, Q6, Q7, Q8, Q9, Q10, Q11, Q12, Q13]), "depth" : 6 * mm});
        }
        {
            var Q0;
            Q0=makeQuery(id+"F10.opExtrude","CAP_EDGE",EDGE,{"disambiguationData":[OSD([sQuery(id+"F2.wireOp",EDGE,"E49.9")])],"isStart":false});
            var Q1;
            Q1=makeQuery(id+"F10.opExtrude","CAP_EDGE",EDGE,{"disambiguationData":[OSD([sQuery(id+"F2.wireOp",EDGE,"E49.10")])],"isStart":false});
            chamfer(context, id + "F11", {"entities" : qUnion([Q0, Q1]), "width" : 3 * mm, "tangentPropagation" : true});
        }
        {
            var Q0;
            Q0=makeQuery(id+"F3.imprint","IMPRINT",FACE,{"disambiguationData":[TD([[makeQuery(id+"F3.imprint","IMPRINT",EDGE,{"derivedFrom":sQuery(id+"F3.wireOp",EDGE,"E93.15")}),-1.0]])]});
            var Q1;
            Q1=makeQuery(id+"F3.imprint","IMPRINT",FACE,{"disambiguationData":[TD([[makeQuery(id+"F3.imprint","IMPRINT",EDGE,{"derivedFrom":sQuery(id+"F3.wireOp",EDGE,"E93.16")}),-1.0]])]});
            var Q2;
            Q2=makeQuery(id+"F3.imprint","IMPRINT",FACE,{"disambiguationData":[TD([[makeQuery(id+"F3.imprint","IMPRINT",EDGE,{"derivedFrom":sQuery(id+"F3.wireOp",EDGE,"E93.13")}),-1.0]])]});
            var Q3;
            Q3=makeQuery(id+"F3.imprint","IMPRINT",FACE,{"disambiguationData":[TD([[makeQuery(id+"F3.imprint","IMPRINT",EDGE,{"derivedFrom":sQuery(id+"F3.wireOp",EDGE,"E93.12")}),-1.0]])]});
            var Q4;
            {var subQ0=sQuery(id+"F3.wireOp",EDGE,"E100");var subQ1=makeQuery(id+"F3.imprint","INTERSECT",VERTEX,{"derivedFrom":[subQ0,sQuery(id+"F3.wireOp",EDGE,"E113.MirrorCS")]});Q4=makeQuery(id+"F3.imprint","IMPRINT",FACE,{"disambiguationData":[TD([[makeQuery(id+"F3.imprint","IMPRINT",EDGE,{"disambiguationData":[TD([[subQ1,-1.0]])],"derivedFrom":subQ0}),1.0]])]});}
            var Q5;
            {var subQ0=sQuery(id+"F3.wireOp",EDGE,"E99");var subQ1=makeQuery(id+"F3.imprint","INTERSECT",VERTEX,{"derivedFrom":[subQ0,sQuery(id+"F3.wireOp",EDGE,"E109.MirrorCS")]});Q5=makeQuery(id+"F3.imprint","IMPRINT",FACE,{"disambiguationData":[TD([[makeQuery(id+"F3.imprint","IMPRINT",EDGE,{"disambiguationData":[TD([[subQ1,1.0]])],"derivedFrom":subQ0}),1.0]])]});}
            var Q6;
            Q6=makeQuery(id+"F3.imprint","IMPRINT",FACE,{"disambiguationData":[TD([[makeQuery(id+"F3.imprint","IMPRINT",EDGE,{"derivedFrom":sQuery(id+"F3.wireOp",EDGE,"E93.2")}),-1.0]])]});
            var Q7;
            Q7=makeQuery(id+"F3.imprint","IMPRINT",FACE,{"disambiguationData":[TD([[makeQuery(id+"F3.imprint","IMPRINT",EDGE,{"derivedFrom":sQuery(id+"F3.wireOp",EDGE,"E93.4")}),-1.0]])]});
            var Q8;
            Q8=makeQuery(id+"F3.imprint","IMPRINT",FACE,{"disambiguationData":[TD([[makeQuery(id+"F3.imprint","IMPRINT",EDGE,{"derivedFrom":sQuery(id+"F3.wireOp",EDGE,"E93.4")}),1.0]])]});
            var Q9;
            {var subQ0=sQuery(id+"F3.wireOp",EDGE,"E116");Q9=makeQuery(id+"F3.imprint","IMPRINT",FACE,{"disambiguationData":[TD([[makeQuery(id+"F3.imprint","IMPRINT",EDGE,{"derivedFrom":subQ0}),1.0]])]});}
            var Q10;
            {var subQ0=sQuery(id+"F3.wireOp",EDGE,"E122");Q10=makeQuery(id+"F3.imprint","IMPRINT",FACE,{"disambiguationData":[TD([[makeQuery(id+"F3.imprint","IMPRINT",EDGE,{"derivedFrom":subQ0}),1.0]])]});}
            var Q11;
            {var subQ0=sQuery(id+"F3.wireOp",EDGE,"E115");Q11=makeQuery(id+"F3.imprint","IMPRINT",FACE,{"disambiguationData":[TD([[makeQuery(id+"F3.imprint","IMPRINT",EDGE,{"derivedFrom":subQ0}),-1.0]])]});}
            var Q12;
            Q12=makeQuery(id+"F3.imprint","IMPRINT",FACE,{"disambiguationData":[TD([[makeQuery(id+"F3.imprint","IMPRINT",EDGE,{"derivedFrom":sQuery(id+"F3.wireOp",EDGE,"E93.0")}),1.0]])]});
            var Q13;
            {var subQ0=sQuery(id+"F3.wireOp",EDGE,"E121");Q13=makeQuery(id+"F3.imprint","IMPRINT",FACE,{"disambiguationData":[TD([[makeQuery(id+"F3.imprint","IMPRINT",EDGE,{"derivedFrom":subQ0}),-1.0]])]});}
            extrude(context, id + "F12", {"entities" : qUnion([Q0, Q1, Q2, Q3, Q4, Q5, Q6, Q7, Q8, Q9, Q10, Q11, Q12, Q13]), "oppositeDirection" : true, "depth" : 25 * mm});
        }
        {
            var Q0;
            Q0=makeQuery(id+"F3.imprint","IMPRINT",FACE,{"disambiguationData":[TD([[makeQuery(id+"F3.imprint","IMPRINT",EDGE,{"derivedFrom":sQuery(id+"F3.wireOp",EDGE,"E93.0")}),1.0]])]});
            var Q1;
            Q1=makeQuery(id+"F3.imprint","IMPRINT",FACE,{"disambiguationData":[TD([[makeQuery(id+"F3.imprint","IMPRINT",EDGE,{"derivedFrom":sQuery(id+"F3.wireOp",EDGE,"E93.3")}),-1.0]])]});
            var Q2;
            Q2=makeQuery(id+"F3.imprint","IMPRINT",FACE,{"disambiguationData":[TD([[makeQuery(id+"F3.imprint","IMPRINT",EDGE,{"derivedFrom":sQuery(id+"F3.wireOp",EDGE,"E93.4")}),1.0]])]});
            var Q3;
            Q3=makeQuery(id+"F3.imprint","IMPRINT",FACE,{"disambiguationData":[TD([[makeQuery(id+"F3.imprint","IMPRINT",EDGE,{"derivedFrom":sQuery(id+"F3.wireOp",EDGE,"E93.3")}),1.0]])]});
            var Q4;
            Q4=makeQuery(id+"F3.imprint","IMPRINT",FACE,{"disambiguationData":[TD([[makeQuery(id+"F3.imprint","IMPRINT",EDGE,{"derivedFrom":sQuery(id+"F3.wireOp",EDGE,"E93.4")}),-1.0]])]});
            var Q5;
            Q5=makeQuery(id+"F3.imprint","IMPRINT",FACE,{"disambiguationData":[TD([[makeQuery(id+"F3.imprint","IMPRINT",EDGE,{"derivedFrom":sQuery(id+"F3.wireOp",EDGE,"E93.2")}),-1.0]])]});
            var Q6;
            Q6=makeQuery(id+"F3.imprint","IMPRINT",FACE,{"disambiguationData":[TD([[makeQuery(id+"F3.imprint","IMPRINT",EDGE,{"derivedFrom":sQuery(id+"F3.wireOp",EDGE,"E95")}),-1.0]])]});
            extrude(context, id + "F13", {"entities" : qUnion([Q0, Q1, Q2, Q3, Q4, Q5, Q6]), "depth" : 6 * mm});
        }
        {
            var Q0;
            Q0=makeQuery(id+"F3.imprint","IMPRINT",FACE,{"disambiguationData":[TD([[makeQuery(id+"F3.imprint","IMPRINT",EDGE,{"derivedFrom":sQuery(id+"F3.wireOp",EDGE,"E93.16")}),1.0]])]});
            var Q1;
            Q1=makeQuery(id+"F3.imprint","IMPRINT",FACE,{"disambiguationData":[TD([[makeQuery(id+"F3.imprint","IMPRINT",EDGE,{"derivedFrom":sQuery(id+"F3.wireOp",EDGE,"E93.12")}),1.0]])]});
            var Q2;
            Q2=makeQuery(id+"F3.imprint","IMPRINT",FACE,{"disambiguationData":[TD([[makeQuery(id+"F3.imprint","IMPRINT",EDGE,{"derivedFrom":sQuery(id+"F3.wireOp",EDGE,"E93.13")}),1.0]])]});
            var Q3;
            Q3=makeQuery(id+"F3.imprint","IMPRINT",FACE,{"disambiguationData":[TD([[makeQuery(id+"F3.imprint","IMPRINT",EDGE,{"derivedFrom":sQuery(id+"F3.wireOp",EDGE,"E93.15")}),1.0]])]});
            extrude(context, id + "F14", {"entities" : qUnion([Q0, Q1, Q2, Q3]), "depth" : 6 * mm, "hasSecondDirection" : true, "secondDirectionBound" : SecondDirectionBoundingType.UP_TO_NEXT, "secondDirectionOppositeDirection" : true, "secondDirectionDepth" : 25 * mm});
        }
        {
            var Q0;
            {var subQ0=sQuery(id+"F3.wireOp",EDGE,"E131");Q0=makeQuery(id+"F3.imprint","IMPRINT",FACE,{"disambiguationData":[TD([[makeQuery(id+"F3.imprint","IMPRINT",EDGE,{"derivedFrom":subQ0}),1.0]])]});}
            extrude(context, id + "F15", {"entities" : qUnion([Q0]), "oppositeDirection" : true, "depth" : 25 * mm});
        }
        {
            var Q0;
            Q0=makeQuery(id+"F2.imprint","IMPRINT",FACE,{"disambiguationData":[TD([[makeQuery(id+"F2.imprint","IMPRINT",EDGE,{"derivedFrom":sQuery(id+"F2.wireOp",EDGE,"E55.0")}),1.0]])]});
            var Q1;
            Q1=makeQuery(id+"F13.opExtrude","CAP_FACE",FACE,{"disambiguationData":[OSD([sQuery(id+"F3.wireOp",EDGE,"E93.0"),sQuery(id+"F3.wireOp",EDGE,"E93.1"),sQuery(id+"F3.wireOp",EDGE,"E93.2"),sQuery(id+"F3.wireOp",EDGE,"E93.3"),sQuery(id+"F3.wireOp",EDGE,"E93.4"),sQuery(id+"F3.wireOp",EDGE,"E93.5"),sQuery(id+"F3.wireOp",EDGE,"E93.6"),sQuery(id+"F3.wireOp",EDGE,"E93.7"),sQuery(id+"F3.wireOp",EDGE,"E93.8"),sQuery(id+"F3.wireOp",EDGE,"E93.9"),sQuery(id+"F3.wireOp",EDGE,"E93.10"),sQuery(id+"F3.wireOp",EDGE,"E93.11"),sQuery(id+"F3.wireOp",EDGE,"E93.14"),sQuery(id+"F3.wireOp",EDGE,"E93.17"),sQuery(id+"F3.wireOp",EDGE,"E95"),sQuery(id+"F3.wireOp",EDGE,"E98"),sQuery(id+"F3.wireOp",EDGE,"E99"),sQuery(id+"F3.wireOp",EDGE,"E100"),sQuery(id+"F3.wireOp",EDGE,"E101"),sQuery(id+"F3.wireOp",EDGE,"E102"),sQuery(id+"F3.wireOp",EDGE,"E103"),sQuery(id+"F3.wireOp",EDGE,"E105"),sQuery(id+"F3.wireOp",EDGE,"E106"),sQuery(id+"F3.wireOp",EDGE,"E107"),sQuery(id+"F3.wireOp",EDGE,"E108"),sQuery(id+"F3.wireOp",EDGE,"E109.MirrorCS"),sQuery(id+"F3.wireOp",EDGE,"E110.MirrorCS"),sQuery(id+"F3.wireOp",EDGE,"E111.MirrorCS"),sQuery(id+"F3.wireOp",EDGE,"E112.MirrorCS"),sQuery(id+"F3.wireOp",EDGE,"E113.MirrorCS"),sQuery(id+"F3.wireOp",EDGE,"E114.MirrorCS")])],"isStart":false});
            extrude(context, id + "F16", {"entities" : qUnion([Q0]), "endBoundEntityFace" : qUnion([Q1]), "depth" : 29 * mm});
        }
        {
            var Q0;
            Q0=makeQuery(id+"F16.opExtrude","CAP_FACE",FACE,{"disambiguationData":[OSD([sQuery(id+"F2.wireOp",EDGE,"E55.0"),sQuery(id+"F2.wireOp",EDGE,"E55.1"),sQuery(id+"F2.wireOp",EDGE,"E55.2"),sQuery(id+"F2.wireOp",EDGE,"E55.3"),sQuery(id+"F2.wireOp",EDGE,"E55.4"),sQuery(id+"F2.wireOp",EDGE,"E58"),sQuery(id+"F2.wireOp",EDGE,"E63"),sQuery(id+"F2.wireOp",EDGE,"E84.0"),sQuery(id+"F2.wireOp",EDGE,"E84.1"),sQuery(id+"F2.wireOp",EDGE,"E84.2"),sQuery(id+"F2.wireOp",EDGE,"E84.3"),sQuery(id+"F2.wireOp",EDGE,"E84.4")])],"isStart":false});
            var sketch = newSketch(context, id + "F17", { "sketchPlane" : qUnion([Q0])});
            skLineSegment(sketch, "E133.0", {"start": v(-215.93, -6) * mm, "end": v(-149.4, -6) * mm});
            skLineSegment(sketch, "E133.1", {"start": v(-215.93, -6) * mm, "end": v(-223, -13.07) * mm});
            skLineSegment(sketch, "E133.2", {"start": v(-223, -13.07) * mm, "end": v(-223, -86.93) * mm});
            skLineSegment(sketch, "E133.3", {"start": v(-215.93, -94) * mm, "end": v(-223, -86.93) * mm});
            skLineSegment(sketch, "E133.4", {"start": v(-215.93, -94) * mm, "end": v(-149.4, -94) * mm});
            skCircle(sketch, "E134.0", {"center": v(-98.5, -50) * mm, "radius": 45 * mm, "construction": true});
            skLineSegment(sketch, "E135", {"start": v(-149.4, -6) * mm, "end": v(-123.4, -6) * mm});
            skLineSegment(sketch, "E136", {"start": v(-123.4, -6) * mm, "end": v(-123.4, -94) * mm});
            skCircle(sketch, "E137.0", {"center": v(-98.5, -50) * mm, "radius": 30 * mm});
            skCircle(sketch, "E138", {"center": v(-98.5, -50) * mm, "radius": 45 * mm});
            skPoint(sketch, "E139", {"position": v(-123.4, -12.52) * mm});
            skPoint(sketch, "E140", {"position": v(-123.4, -87.48) * mm});
            skLineSegment(sketch, "E141", {"start": v(-149.4, -94) * mm, "end": v(-123.4, -94) * mm});
            skCircle(sketch, "E142.0", {"center": v(-128.69, -1) * mm, "radius": 2.5 * mm});
            skLineSegment(sketch, "E143.0", {"start": v(-88, 4) * mm, "end": v(-149.4, 4) * mm});
            skLineSegment(sketch, "E143.1", {"start": v(-149.4, -104) * mm, "end": v(-88, -104) * mm});
            skLineSegment(sketch, "E144", {"start": v(-123.4, -6) * mm, "end": v(-123.4, 4) * mm});
            skLineSegment(sketch, "E145", {"start": v(-123.4, 4) * mm, "end": v(-149.4, 4) * mm});
            skLineSegment(sketch, "E146", {"start": v(-149.4, 4) * mm, "end": v(-149.4, -6) * mm});
            skLineSegment(sketch, "E147", {"start": v(-149.4, -94) * mm, "end": v(-149.4, -104) * mm});
            skLineSegment(sketch, "E148", {"start": v(-123.4, -104) * mm, "end": v(-123.4, -94) * mm});
            skLineSegment(sketch, "E149.0", {"start": v(-144.69, 1.5) * mm, "end": v(-128.69, 1.5) * mm});
            skCircle(sketch, "E149.1", {"center": v(-144.69, -1) * mm, "radius": 2.5 * mm});
            skLineSegment(sketch, "E149.2", {"start": v(-144.69, -3.5) * mm, "end": v(-128.69, -3.5) * mm});
            skLineSegment(sketch, "E150.0", {"start": v(-144.69, -96.5) * mm, "end": v(-128.69, -96.5) * mm});
            skLineSegment(sketch, "E150.1", {"start": v(-144.69, -101.5) * mm, "end": v(-128.69, -101.5) * mm});
            skCircle(sketch, "E150.2", {"center": v(-144.69, -99) * mm, "radius": 2.5 * mm});
            skCircle(sketch, "E150.3", {"center": v(-128.69, -99) * mm, "radius": 2.5 * mm});
            skCircle(sketch, "E151.0", {"center": v(-178.5, -50) * mm, "radius": 25 * mm});
            skCircle(sketch, "E152", {"center": v(-178.5, -50) * mm, "radius": 22 * mm});
            skLineSegment(sketch, "E153", {"start": v(-143.5, -6) * mm, "end": v(-143.5, -94) * mm});
            skLineSegment(sketch, "E154", {"start": v(-149.4, -8) * mm, "end": v(-149.4, -92) * mm});
            skLineSegment(sketch, "E155", {"start": v(-149.4, -8) * mm, "end": v(-123.4, -8) * mm});
            skLineSegment(sketch, "E156", {"start": v(-149.4, -92) * mm, "end": v(-123.4, -92) * mm});
            skLineSegment(sketch, "E157", {"start": v(-128.5, -8) * mm, "end": v(-128.5, -92) * mm});
            skSolve(sketch);
        }
        {
            var Q0;
            Q0=makeQuery(id+"F17.imprint","IMPRINT",FACE,{"disambiguationData":[TD([[makeQuery(id+"F17.imprint","IMPRINT",EDGE,{"derivedFrom":sQuery(id+"F17.wireOp",EDGE,"E133.0")}),-1.0]])]});
            var Q1;
            Q1=makeQuery(id+"F17.imprint","IMPRINT",FACE,{"disambiguationData":[TD([[makeQuery(id+"F17.imprint","IMPRINT",EDGE,{"derivedFrom":sQuery(id+"F17.wireOp",EDGE,"E151.0")}),1.0]])]});
            var Q2;
            Q2=makeQuery(id+"F17.imprint","IMPRINT",FACE,{"disambiguationData":[TD([[makeQuery(id+"F17.imprint","IMPRINT",EDGE,{"derivedFrom":sQuery(id+"F17.wireOp",EDGE,"E151.0")}),-1.0]])]});
            var Q3;
            {var subQ1=sQuery(id+"F17.wireOp",EDGE,"E154");Q3=makeQuery(id+"F17.imprint","IMPRINT",FACE,{"disambiguationData":[TD([[makeQuery(id+"F17.imprint","IMPRINT",EDGE,{"derivedFrom":subQ1}),1.0]])]});}
            var Q4;
            {var subQ0=sQuery(id+"F17.wireOp",EDGE,"E157");var subQ1=sQuery(id+"F17.wireOp",EDGE,"E138");var subQ2=makeQuery(id+"F17.imprint","INTERSECT",VERTEX,{"disambiguationData":[OD(0.0)],"derivedFrom":[subQ1,subQ0]});Q4=makeQuery(id+"F17.imprint","IMPRINT",FACE,{"disambiguationData":[TD([[makeQuery(id+"F17.imprint","IMPRINT",EDGE,{"disambiguationData":[TD([[subQ2,-1.0]])],"derivedFrom":subQ1}),1.0]])]});}
            var Q5;
            {var subQ0=sQuery(id+"F17.wireOp",EDGE,"E157");var subQ1=sQuery(id+"F17.wireOp",EDGE,"E138");var subQ2=makeQuery(id+"F17.imprint","INTERSECT",VERTEX,{"disambiguationData":[OD(0.0)],"derivedFrom":[subQ1,subQ0]});Q5=makeQuery(id+"F17.imprint","IMPRINT",FACE,{"disambiguationData":[TD([[makeQuery(id+"F17.imprint","IMPRINT",EDGE,{"disambiguationData":[TD([[subQ2,-1.0]])],"derivedFrom":subQ1}),-1.0]])]});}
            var Q6;
            {var subQ0=sQuery(id+"F17.wireOp",EDGE,"E153");var subQ1=sQuery(id+"F17.wireOp",EDGE,"E138");var subQ2=makeQuery(id+"F17.imprint","INTERSECT",VERTEX,{"derivedFrom":[subQ1,subQ0]});Q6=makeQuery(id+"F17.imprint","IMPRINT",FACE,{"disambiguationData":[TD([[makeQuery(id+"F17.imprint","IMPRINT",EDGE,{"disambiguationData":[TD([[subQ2,-1.0]])],"derivedFrom":subQ1}),-1.0]])]});}
            var Q7;
            Q7=makeQuery(id+"F13.opExtrude","CAP_FACE",FACE,{"disambiguationData":[OSD([sQuery(id+"F3.wireOp",EDGE,"E93.0"),sQuery(id+"F3.wireOp",EDGE,"E93.1"),sQuery(id+"F3.wireOp",EDGE,"E93.2"),sQuery(id+"F3.wireOp",EDGE,"E93.3"),sQuery(id+"F3.wireOp",EDGE,"E93.4"),sQuery(id+"F3.wireOp",EDGE,"E93.5"),sQuery(id+"F3.wireOp",EDGE,"E93.6"),sQuery(id+"F3.wireOp",EDGE,"E93.7"),sQuery(id+"F3.wireOp",EDGE,"E93.8"),sQuery(id+"F3.wireOp",EDGE,"E93.9"),sQuery(id+"F3.wireOp",EDGE,"E93.10"),sQuery(id+"F3.wireOp",EDGE,"E93.11"),sQuery(id+"F3.wireOp",EDGE,"E93.14"),sQuery(id+"F3.wireOp",EDGE,"E93.17"),sQuery(id+"F3.wireOp",EDGE,"E95"),sQuery(id+"F3.wireOp",EDGE,"E98"),sQuery(id+"F3.wireOp",EDGE,"E99"),sQuery(id+"F3.wireOp",EDGE,"E100"),sQuery(id+"F3.wireOp",EDGE,"E101"),sQuery(id+"F3.wireOp",EDGE,"E102"),sQuery(id+"F3.wireOp",EDGE,"E103"),sQuery(id+"F3.wireOp",EDGE,"E105"),sQuery(id+"F3.wireOp",EDGE,"E106"),sQuery(id+"F3.wireOp",EDGE,"E107"),sQuery(id+"F3.wireOp",EDGE,"E108"),sQuery(id+"F3.wireOp",EDGE,"E109.MirrorCS"),sQuery(id+"F3.wireOp",EDGE,"E110.MirrorCS"),sQuery(id+"F3.wireOp",EDGE,"E111.MirrorCS"),sQuery(id+"F3.wireOp",EDGE,"E112.MirrorCS"),sQuery(id+"F3.wireOp",EDGE,"E113.MirrorCS"),sQuery(id+"F3.wireOp",EDGE,"E114.MirrorCS")])],"isStart":false});
            extrude(context, id + "F18", {"entities" : qUnion([Q0, Q1, Q2, Q3, Q4, Q5, Q6]), "endBoundEntityFace" : qUnion([Q7]), "depth" : 2 * mm});
        }
        {
            var Q0;
            {var subQ0=sQuery(id+"F2.wireOp",EDGE,"E86");Q0=makeQuery(id+"F2.imprint","IMPRINT",FACE,{"disambiguationData":[TD([[makeQuery(id+"F2.imprint","IMPRINT",EDGE,{"derivedFrom":subQ0}),1.0]])]});}
            var Q1;
            Q1=makeQuery(id+"F10.opExtrude","CAP_FACE",FACE,{"disambiguationData":[OSD([sQuery(id+"F2.wireOp",EDGE,"E49.7"),sQuery(id+"F2.wireOp",EDGE,"E49.8"),sQuery(id+"F2.wireOp",EDGE,"E49.9"),sQuery(id+"F2.wireOp",EDGE,"E49.10"),sQuery(id+"F2.wireOp",EDGE,"E49.11"),sQuery(id+"F2.wireOp",EDGE,"E49.12"),sQuery(id+"F2.wireOp",EDGE,"E49.18"),sQuery(id+"F2.wireOp",EDGE,"E55.0"),sQuery(id+"F2.wireOp",EDGE,"E55.1"),sQuery(id+"F2.wireOp",EDGE,"E55.2"),sQuery(id+"F2.wireOp",EDGE,"E55.3"),sQuery(id+"F2.wireOp",EDGE,"E55.4"),sQuery(id+"F2.wireOp",EDGE,"E56.0"),sQuery(id+"F2.wireOp",EDGE,"E56.1"),sQuery(id+"F2.wireOp",EDGE,"E57.0"),sQuery(id+"F2.wireOp",EDGE,"E57.1"),sQuery(id+"F2.wireOp",EDGE,"E58"),sQuery(id+"F2.wireOp",EDGE,"E59"),sQuery(id+"F2.wireOp",EDGE,"E61"),sQuery(id+"F2.wireOp",EDGE,"E63"),sQuery(id+"F2.wireOp",EDGE,"E64"),sQuery(id+"F2.wireOp",EDGE,"E65"),sQuery(id+"F2.wireOp",EDGE,"E66"),sQuery(id+"F2.wireOp",EDGE,"E72"),sQuery(id+"F2.wireOp",EDGE,"E73"),sQuery(id+"F2.wireOp",EDGE,"E74"),sQuery(id+"F2.wireOp",EDGE,"E75"),sQuery(id+"F2.wireOp",EDGE,"E80"),sQuery(id+"F2.wireOp",EDGE,"E81"),sQuery(id+"F2.wireOp",EDGE,"E82"),sQuery(id+"F2.wireOp",EDGE,"E83.0")])],"isStart":false});
            extrude(context, id + "F19", {"entities" : qUnion([Q0]), "operationType" : NewBodyOperationType.REMOVE, "endBound" : BoundingType.UP_TO_SURFACE, "endBoundEntityFace" : qUnion([Q1]), "depth" : 25 * mm});
        }
        {
            var Q0;
            Q0=makeQuery(id+"F10.opExtrude","CAP_FACE",FACE,{"disambiguationData":[OSD([sQuery(id+"F2.wireOp",EDGE,"E49.7"),sQuery(id+"F2.wireOp",EDGE,"E49.8"),sQuery(id+"F2.wireOp",EDGE,"E49.9"),sQuery(id+"F2.wireOp",EDGE,"E49.10"),sQuery(id+"F2.wireOp",EDGE,"E49.11"),sQuery(id+"F2.wireOp",EDGE,"E49.12"),sQuery(id+"F2.wireOp",EDGE,"E49.18"),sQuery(id+"F2.wireOp",EDGE,"E55.0"),sQuery(id+"F2.wireOp",EDGE,"E55.1"),sQuery(id+"F2.wireOp",EDGE,"E55.2"),sQuery(id+"F2.wireOp",EDGE,"E55.3"),sQuery(id+"F2.wireOp",EDGE,"E55.4"),sQuery(id+"F2.wireOp",EDGE,"E56.0"),sQuery(id+"F2.wireOp",EDGE,"E56.1"),sQuery(id+"F2.wireOp",EDGE,"E57.0"),sQuery(id+"F2.wireOp",EDGE,"E57.1"),sQuery(id+"F2.wireOp",EDGE,"E58"),sQuery(id+"F2.wireOp",EDGE,"E59"),sQuery(id+"F2.wireOp",EDGE,"E61"),sQuery(id+"F2.wireOp",EDGE,"E63"),sQuery(id+"F2.wireOp",EDGE,"E65"),sQuery(id+"F2.wireOp",EDGE,"E72"),sQuery(id+"F2.wireOp",EDGE,"E73"),sQuery(id+"F2.wireOp",EDGE,"E74"),sQuery(id+"F2.wireOp",EDGE,"E75"),sQuery(id+"F2.wireOp",EDGE,"E80"),sQuery(id+"F2.wireOp",EDGE,"E81"),sQuery(id+"F2.wireOp",EDGE,"E82"),sQuery(id+"F2.wireOp",EDGE,"E83.0"),sQuery(id+"F2.wireOp",EDGE,"E87.MirrorCS"),sQuery(id+"F2.wireOp",EDGE,"E89.MirrorC"),sQuery(id+"F2.wireOp",EDGE,"E90.MirrorC"),sQuery(id+"F2.wireOp",EDGE,"E92")])],"isStart":false});
            var sketch = newSketch(context, id + "F20", { "sketchPlane" : qUnion([Q0])});
            skLineSegment(sketch, "E158.0", {"start": v(-178.5, -25) * mm, "end": v(-178.5, -8) * mm, "construction": true});
            skLineSegment(sketch, "E159.0", {"start": v(-215.1, -8) * mm, "end": v(-149.4, -8) * mm});
            skLineSegment(sketch, "E160", {"start": v(-173.5, -8) * mm, "end": v(-173.5, -25.5) * mm});
            skLineSegment(sketch, "E161.MirrorCS", {"start": v(-183.5, -8) * mm, "end": v(-183.5, -25.5) * mm});
            skLineSegment(sketch, "E162", {"start": v(-183.5, -25.5) * mm, "end": v(-173.5, -25.5) * mm});
            skCircle(sketch, "E163.0", {"center": v(-178.5, -50) * mm, "radius": 25 * mm});
            skSolve(sketch);
        }
        {
            var Q0;
            {var subQ2=sQuery(id+"F20.wireOp",EDGE,"E161.MirrorCS");Q0=makeQuery(id+"F20.imprint","IMPRINT",FACE,{"disambiguationData":[TD([[makeQuery(id+"F20.imprint","IMPRINT",EDGE,{"derivedFrom":subQ2}),1.0]])]});}
            var Q1;
            {var subQ3=sQuery(id+"F20.wireOp",EDGE,"E160");Q1=makeQuery(id+"F20.imprint","IMPRINT",FACE,{"disambiguationData":[TD([[makeQuery(id+"F20.imprint","IMPRINT",EDGE,{"derivedFrom":subQ3}),-1.0]])]});}
            var Q2;
            {var subQ1=makeQuery(id+"F19.boolean.opBoolean","COPY",EDGE,{"derivedFrom":makeQuery(id+"F19.opExtrude","CAP_EDGE",EDGE,{"disambiguationData":[OSD([sQuery(id+"F2.wireOp",EDGE,"E86")])],"isStart":false})});Q2=makeQuery(id+"F20.imprint","IMPRINT",FACE,{"disambiguationData":[TD([[makeQuery(id+"F20.imprint","IMPRINT",EDGE,{"derivedFrom":subQ1}),1.0]])]});}
            extrude(context, id + "F21", {"entities" : qUnion([Q0, Q1, Q2]), "depth" : 1 * mm});
        }
        {
            var Q0;
            {var subQ0=sQuery(id+"F1.wireOp",EDGE,"E35");Q0=makeQuery(id+"F1.imprint","IMPRINT",FACE,{"disambiguationData":[TD([[makeQuery(id+"F1.imprint","IMPRINT",EDGE,{"derivedFrom":subQ0}),1.0]])]});}
            var Q1;
            {var subQ4=sQuery(id+"F1.wireOp",EDGE,"E42");Q1=makeQuery(id+"F1.imprint","IMPRINT",FACE,{"disambiguationData":[TD([[makeQuery(id+"F1.imprint","IMPRINT",EDGE,{"derivedFrom":subQ4}),-1.0]])]});}
            var Q2;
            {var subQ2=sQuery(id+"F1.wireOp",EDGE,"E39.MirrorCS");Q2=makeQuery(id+"F1.imprint","IMPRINT",FACE,{"disambiguationData":[TD([[makeQuery(id+"F1.imprint","IMPRINT",EDGE,{"derivedFrom":subQ2}),-1.0]])]});}
            extrude(context, id + "F22", {"entities" : qUnion([Q0, Q1, Q2]), "depth" : 8 * mm});
        }
        {
            var Q0;
            {var subQ0=sQuery(id+"F1.wireOp",EDGE,"E38");Q0=makeQuery(id+"F1.imprint","IMPRINT",FACE,{"disambiguationData":[TD([[makeQuery(id+"F1.imprint","IMPRINT",EDGE,{"derivedFrom":subQ0}),-1.0]])]});}
            var Q1;
            {var subQ0=sQuery(id+"F1.wireOp",EDGE,"E39.MirrorCS");Q1=makeQuery(id+"F1.imprint","IMPRINT",FACE,{"disambiguationData":[TD([[makeQuery(id+"F1.imprint","IMPRINT",EDGE,{"derivedFrom":subQ0}),1.0]])]});}
            extrude(context, id + "F23", {"entities" : qUnion([Q0, Q1]), "depth" : 20 * mm});
        }
        {
            var Q0;
            Q0=makeQuery(id+"F23.opExtrude","SWEPT_FACE",FACE,{"disambiguationData":[OSD([sQuery(id+"F1.wireOp",EDGE,"E39.MirrorCS")])]});
            var sketch = newSketch(context, id + "F24", { "sketchPlane" : qUnion([Q0])});
            skLineSegment(sketch, "E164.0", {"start": v(-32.12, 20) * mm, "end": v(-20.12, 20) * mm});
            skLineSegment(sketch, "E165", {"start": v(-32.12, 20) * mm, "end": v(-32.12, 8) * mm});
            skLineSegment(sketch, "E166", {"start": v(-32.12, 8) * mm, "end": v(-20.12, 8) * mm});
            skLineSegment(sketch, "E167", {"start": v(-20.12, 8) * mm, "end": v(-20.12, 20) * mm});
            skCircle(sketch, "E168", {"center": v(-26.12, 14) * mm, "radius": 3 * mm});
            skPoint(sketch, "E168.centerSnap0", {"position": v(-26.12, 20) * mm});
            skPoint(sketch, "E168.centerSnap1", {"position": v(-32.12, 14) * mm});
            skSolve(sketch);
        }
        {
            var Q0;
            Q0=makeQuery(id+"F24.imprint","IMPRINT",FACE,{"disambiguationData":[TD([[makeQuery(id+"F24.imprint","IMPRINT",EDGE,{"derivedFrom":sQuery(id+"F24.wireOp",EDGE,"E168")}),1.0]])]});
            var Q1;
            Q1=makeQuery(id+"F23.opExtrude","SWEPT_FACE",FACE,{"disambiguationData":[OSD([sQuery(id+"F1.wireOp",EDGE,"E38")])]});
            extrude(context, id + "F25", {"entities" : qUnion([Q0]), "operationType" : NewBodyOperationType.REMOVE, "endBound" : BoundingType.UP_TO_SURFACE, "oppositeDirection" : true, "endBoundEntityFace" : qUnion([Q1]), "depth" : 25 * mm});
        }
        {
            var Q0;
            Q0=makeQuery(id+"F1.imprint","IMPRINT",FACE,{"disambiguationData":[TD([[makeQuery(id+"F1.imprint","IMPRINT",EDGE,{"derivedFrom":sQuery(id+"F1.wireOp",EDGE,"E47.MirrorC")}),-1.0]])]});
            var Q1;
            Q1=makeQuery(id+"F1.imprint","IMPRINT",FACE,{"disambiguationData":[TD([[makeQuery(id+"F1.imprint","IMPRINT",EDGE,{"derivedFrom":sQuery(id+"F1.wireOp",EDGE,"E48")}),1.0]])]});
            var Q2;
            Q2=makeQuery(id+"F1.imprint","IMPRINT",FACE,{"disambiguationData":[TD([[makeQuery(id+"F1.imprint","IMPRINT",EDGE,{"derivedFrom":sQuery(id+"F1.wireOp",EDGE,"E46")}),1.0]])]});
            extrude(context, id + "F26", {"entities" : qUnion([Q0, Q1, Q2]), "operationType" : NewBodyOperationType.REMOVE, "oppositeDirection" : true, "depth" : 10 * mm});
        }
        {
            var Q0;
            Q0=makeQuery(id+"F1.imprint","IMPRINT",FACE,{"disambiguationData":[TD([[makeQuery(id+"F1.imprint","IMPRINT",EDGE,{"derivedFrom":sQuery(id+"F1.wireOp",EDGE,"E47.MirrorC")}),-1.0]])]});
            var Q1;
            Q1=makeQuery(id+"F1.imprint","IMPRINT",FACE,{"disambiguationData":[TD([[makeQuery(id+"F1.imprint","IMPRINT",EDGE,{"derivedFrom":sQuery(id+"F1.wireOp",EDGE,"E48")}),1.0]])]});
            var Q2;
            Q2=makeQuery(id+"F1.imprint","IMPRINT",FACE,{"disambiguationData":[TD([[makeQuery(id+"F1.imprint","IMPRINT",EDGE,{"derivedFrom":sQuery(id+"F1.wireOp",EDGE,"E46")}),1.0]])]});
            extrude(context, id + "F27", {"entities" : qUnion([Q0, Q1, Q2]), "endBound" : BoundingType.SYMMETRIC, "depth" : 16 * mm});
        }
        {
            var Q0;
            Q0=makeQuery(id+"F24.imprint","IMPRINT",FACE,{"disambiguationData":[TD([[makeQuery(id+"F24.imprint","IMPRINT",EDGE,{"derivedFrom":sQuery(id+"F24.wireOp",EDGE,"E168")}),1.0]])]});
            var Q1;
            Q1=makeQuery(id+"F23.opExtrude","SWEPT_FACE",FACE,{"disambiguationData":[OSD([sQuery(id+"F1.wireOp",EDGE,"E38")])]});
            extrude(context, id + "F28", {"entities" : qUnion([Q0]), "endBound" : BoundingType.UP_TO_SURFACE, "oppositeDirection" : true, "endBoundEntityFace" : qUnion([Q1]), "depth" : 25 * mm});
        }
        {
            var Q0;
            Q0=makeQuery(id+"F1.imprint","IMPRINT",FACE,{"disambiguationData":[TD([[makeQuery(id+"F1.imprint","IMPRINT",EDGE,{"derivedFrom":sQuery(id+"F1.wireOp",EDGE,"E0")}),1.0]])]});
            var sketch = newSketch(context, id + "F29", { "sketchPlane" : qUnion([Q0])});
            skLineSegment(sketch, "E169.1", {"start": v(-12.12, -13) * mm, "end": v(0, -20) * mm});
            skLineSegment(sketch, "E169.2", {"start": v(-12.12, -35) * mm, "end": v(-12.12, -13) * mm});
            skLineSegment(sketch, "E169.3", {"start": v(-20.12, -35) * mm, "end": v(-12.12, -35) * mm});
            skLineSegment(sketch, "E169.4", {"start": v(-20.12, -60) * mm, "end": v(-20.12, -35) * mm});
            skLineSegment(sketch, "E169.5", {"start": v(-12.12, -60) * mm, "end": v(-20.12, -60) * mm});
            skLineSegment(sketch, "E169.6", {"start": v(-12.12, -87) * mm, "end": v(-12.12, -60) * mm});
            skLineSegment(sketch, "E169.7", {"start": v(0, -80) * mm, "end": v(-12.12, -87) * mm});
            skLineSegment(sketch, "E169.8", {"start": v(0, -100) * mm, "end": v(0, -80) * mm});
            skLineSegment(sketch, "E170", {"start": v(-12.12, -82) * mm, "end": v(0, -75) * mm});
            skLineSegment(sketch, "E171", {"start": v(0, -75) * mm, "end": v(0, -80) * mm});
            skLineSegment(sketch, "E172", {"start": v(0, 4.75) * mm, "end": v(4, 15) * mm});
            skLineSegment(sketch, "E173", {"start": v(4, 15) * mm, "end": v(48, 15) * mm});
            skLineSegment(sketch, "E174", {"start": v(48, 15) * mm, "end": v(48, -100) * mm});
            skLineSegment(sketch, "E175", {"start": v(48, -100) * mm, "end": v(0, -100) * mm});
            skLineSegment(sketch, "E176", {"start": v(0, -100) * mm, "end": v(0, -100) * mm});
            skLineSegment(sketch, "E177", {"start": v(0, 4.75) * mm, "end": v(0, -20) * mm});
            skLineSegment(sketch, "E178", {"start": v(-12.12, -35) * mm, "end": v(-12.12, -37.5) * mm});
            skLineSegment(sketch, "E179", {"start": v(-12.12, -37.5) * mm, "end": v(-7.12, -37.5) * mm});
            skLineSegment(sketch, "E180", {"start": v(-7.12, -37.5) * mm, "end": v(-7.12, -57.5) * mm});
            skLineSegment(sketch, "E181", {"start": v(-7.12, -57.5) * mm, "end": v(-12.12, -57.5) * mm});
            skLineSegment(sketch, "E182", {"start": v(-12.12, -57.5) * mm, "end": v(-12.12, -60) * mm});
            skLineSegment(sketch, "E183", {"start": v(-12.12, -37.5) * mm, "end": v(-12.12, -57.5) * mm});
            skLineSegment(sketch, "E184", {"start": v(-12.12, -37.5) * mm, "end": v(-14.12, -37.5) * mm});
            skLineSegment(sketch, "E185", {"start": v(-14.12, -37.5) * mm, "end": v(-14.12, -57.5) * mm});
            skLineSegment(sketch, "E186", {"start": v(-14.12, -57.5) * mm, "end": v(-12.12, -57.5) * mm});
            skLineSegment(sketch, "E187.MirrorCS", {"start": v(0, -104.75) * mm, "end": v(4, -115) * mm});
            skLineSegment(sketch, "E188.MirrorCS", {"start": v(4, -115) * mm, "end": v(48, -115) * mm});
            skLineSegment(sketch, "E189", {"start": v(48, -115) * mm, "end": v(48, -100) * mm});
            skLineSegment(sketch, "E190", {"start": v(0, -104.75) * mm, "end": v(0, -100) * mm});
            skLineSegment(sketch, "E191", {"start": v(-32.12, -50) * mm, "end": v(48, -50) * mm, "construction": true});
            skPoint(sketch, "E192", {"position": v(48, -42.5) * mm});
            skLineSegment(sketch, "E193", {"start": v(-14.12, -50) * mm, "end": v(-7.12, -50) * mm});
            skSolve(sketch);
        }
        {
            var Q0;
            {var subQ0=sQuery(id+"F29.wireOp",EDGE,"E169.1");Q0=makeQuery(id+"F29.imprint","IMPRINT",FACE,{"disambiguationData":[TD([[makeQuery(id+"F29.imprint","IMPRINT",EDGE,{"derivedFrom":subQ0}),-1.0]])]});}
            extrude(context, id + "F30", {"entities" : qUnion([Q0]), "depth" : 20 * mm, "hasSecondDirection" : true, "secondDirectionOppositeDirection" : true, "secondDirectionDepth" : 510 * mm});
        }
        {
            var Q0;
            {var subQ0=sQuery(id+"F29.wireOp",EDGE,"E169.7");Q0=makeQuery(id+"F29.imprint","IMPRINT",FACE,{"disambiguationData":[TD([[makeQuery(id+"F29.imprint","IMPRINT",EDGE,{"derivedFrom":subQ0}),-1.0]])]});}
            var Q1;
            Q1=makeQuery(id+"F4.opExtrude","CAP_FACE",FACE,{"disambiguationData":[OSD([sQuery(id+"F1.wireOp",EDGE,"E0"),sQuery(id+"F1.wireOp",EDGE,"E1"),sQuery(id+"F1.wireOp",EDGE,"E5"),sQuery(id+"F1.wireOp",EDGE,"E6"),sQuery(id+"F1.wireOp",EDGE,"E7"),sQuery(id+"F1.wireOp",EDGE,"E8"),sQuery(id+"F1.wireOp",EDGE,"E9"),sQuery(id+"F1.wireOp",EDGE,"E10"),sQuery(id+"F1.wireOp",EDGE,"E12"),sQuery(id+"F1.wireOp",EDGE,"E13"),sQuery(id+"F1.wireOp",EDGE,"E14"),sQuery(id+"F1.wireOp",EDGE,"E15"),sQuery(id+"F1.wireOp",EDGE,"E34"),sQuery(id+"F1.wireOp",EDGE,"E35"),sQuery(id+"F1.wireOp",EDGE,"E36"),sQuery(id+"F1.wireOp",EDGE,"E37"),sQuery(id+"F1.wireOp",EDGE,"E40.MirrorCS"),sQuery(id+"F1.wireOp",EDGE,"E41")])],"isStart":false});
            extrude(context, id + "F31", {"entities" : qUnion([Q0]), "endBound" : BoundingType.UP_TO_SURFACE, "oppositeDirection" : true, "endBoundEntityFace" : qUnion([Q1]), "depth" : 25 * mm});
        }
        {
            var Q0;
            Q0=makeQuery(id+"F29.imprint","IMPRINT",FACE,{"disambiguationData":[TD([[makeQuery(id+"F29.imprint","IMPRINT",EDGE,{"derivedFrom":sQuery(id+"F29.wireOp",EDGE,"E179")}),-1.0]])]});
            var Q1;
            Q1=makeQuery(id+"F29.imprint","IMPRINT",FACE,{"disambiguationData":[TD([[makeQuery(id+"F29.imprint","IMPRINT",EDGE,{"derivedFrom":sQuery(id+"F29.wireOp",EDGE,"E183")}),-1.0]])]});
            var Q2;
            {var subQ0=sQuery(id+"F29.wireOp",EDGE,"E181");Q2=makeQuery(id+"F29.imprint","IMPRINT",FACE,{"disambiguationData":[TD([[makeQuery(id+"F29.imprint","IMPRINT",EDGE,{"derivedFrom":subQ0}),-1.0]])]});}
            var Q3;
            Q3=makeQuery(id+"F4.opExtrude","CAP_FACE",FACE,{"disambiguationData":[OSD([sQuery(id+"F1.wireOp",EDGE,"E0"),sQuery(id+"F1.wireOp",EDGE,"E1"),sQuery(id+"F1.wireOp",EDGE,"E5"),sQuery(id+"F1.wireOp",EDGE,"E6"),sQuery(id+"F1.wireOp",EDGE,"E7"),sQuery(id+"F1.wireOp",EDGE,"E8"),sQuery(id+"F1.wireOp",EDGE,"E9"),sQuery(id+"F1.wireOp",EDGE,"E10"),sQuery(id+"F1.wireOp",EDGE,"E12"),sQuery(id+"F1.wireOp",EDGE,"E13"),sQuery(id+"F1.wireOp",EDGE,"E14"),sQuery(id+"F1.wireOp",EDGE,"E15"),sQuery(id+"F1.wireOp",EDGE,"E34"),sQuery(id+"F1.wireOp",EDGE,"E35"),sQuery(id+"F1.wireOp",EDGE,"E36"),sQuery(id+"F1.wireOp",EDGE,"E37"),sQuery(id+"F1.wireOp",EDGE,"E40.MirrorCS"),sQuery(id+"F1.wireOp",EDGE,"E41")])],"isStart":false});
            extrude(context, id + "F32", {"entities" : qUnion([Q0, Q1, Q2]), "oppositeDirection" : true, "endBoundEntityFace" : qUnion([Q3]), "depth" : 380 * mm});
        }
        {
            var Q0;
            Q0=sQuery(id+"F1.wireOp",VERTEX,"E48.centerSnap1");
            var Q1;
            Q1=sQuery(id+"F1.wireOp",EDGE,"E37");
            cPlane(context, id + "F33", {"entities" : qUnion([Q0, Q1]), "cplaneType" : CPlaneType.LINE_POINT, "offset" : 150 * mm, "width" : 150 * mm, "height" : 150 * mm});
        }
        {
            var Q0;
            Q0=makeQuery(id+"F29.imprint","IMPRINT",FACE,{"disambiguationData":[TD([[makeQuery(id+"F29.imprint","IMPRINT",EDGE,{"derivedFrom":sQuery(id+"F29.wireOp",EDGE,"E179")}),-1.0]])]});
            var Q1;
            Q1=makeQuery(id+"F29.imprint","IMPRINT",FACE,{"disambiguationData":[TD([[makeQuery(id+"F29.imprint","IMPRINT",EDGE,{"derivedFrom":sQuery(id+"F29.wireOp",EDGE,"E183")}),-1.0]])]});
            var Q2;
            Q2=makeQuery(id+"F29.imprint","IMPRINT",FACE,{"disambiguationData":[TD([[makeQuery(id+"F29.imprint","IMPRINT",EDGE,{"derivedFrom":sQuery(id+"F29.wireOp",EDGE,"E169.3")}),-1.0]])]});
            var Q3;
            {var subQ0=sQuery(id+"F29.wireOp",EDGE,"E181");Q3=makeQuery(id+"F29.imprint","IMPRINT",FACE,{"disambiguationData":[TD([[makeQuery(id+"F29.imprint","IMPRINT",EDGE,{"derivedFrom":subQ0}),-1.0]])]});}
            var Q4;
            Q4=makeQuery(id+"F30.opExtrude","CAP_FACE",FACE,{"disambiguationData":[OSD([sQuery(id+"F29.wireOp",EDGE,"E169.1"),sQuery(id+"F29.wireOp",EDGE,"E169.2"),sQuery(id+"F29.wireOp",EDGE,"E169.6"),sQuery(id+"F29.wireOp",EDGE,"E169.8"),sQuery(id+"F29.wireOp",EDGE,"E170"),sQuery(id+"F29.wireOp",EDGE,"E171"),sQuery(id+"F29.wireOp",EDGE,"E172"),sQuery(id+"F29.wireOp",EDGE,"E173"),sQuery(id+"F29.wireOp",EDGE,"E174"),sQuery(id+"F29.wireOp",EDGE,"E175"),sQuery(id+"F29.wireOp",EDGE,"E177"),sQuery(id+"F29.wireOp",EDGE,"E178"),sQuery(id+"F29.wireOp",EDGE,"E179"),sQuery(id+"F29.wireOp",EDGE,"E180"),sQuery(id+"F29.wireOp",EDGE,"E181"),sQuery(id+"F29.wireOp",EDGE,"E182")])],"isStart":false});
            var Q5;
            Q5=makeQuery(id+"F30.opExtrude","CAP_FACE",FACE,{"disambiguationData":[OSD([sQuery(id+"F29.wireOp",EDGE,"E169.1"),sQuery(id+"F29.wireOp",EDGE,"E169.2"),sQuery(id+"F29.wireOp",EDGE,"E169.6"),sQuery(id+"F29.wireOp",EDGE,"E169.8"),sQuery(id+"F29.wireOp",EDGE,"E170"),sQuery(id+"F29.wireOp",EDGE,"E171"),sQuery(id+"F29.wireOp",EDGE,"E172"),sQuery(id+"F29.wireOp",EDGE,"E173"),sQuery(id+"F29.wireOp",EDGE,"E174"),sQuery(id+"F29.wireOp",EDGE,"E175"),sQuery(id+"F29.wireOp",EDGE,"E177"),sQuery(id+"F29.wireOp",EDGE,"E178"),sQuery(id+"F29.wireOp",EDGE,"E179"),sQuery(id+"F29.wireOp",EDGE,"E180"),sQuery(id+"F29.wireOp",EDGE,"E181"),sQuery(id+"F29.wireOp",EDGE,"E182")])],"isStart":true});
            extrude(context, id + "F34", {"entities" : qUnion([Q0, Q1, Q2, Q3]), "operationType" : NewBodyOperationType.REMOVE, "oppositeDirection" : true, "endBoundEntityFace" : qUnion([Q4]), "depth" : 50 * mm});
        }
        {
            var Q0;
            Q0=qCreatedBy(id+"F33.planeOp",FACE);
            var sketch = newSketch(context, id + "F35", { "sketchPlane" : qUnion([Q0])});
            skArc(sketch, "E194", {"start": v(-1.12, 95) * mm, "mid": v(-18.8, 87.68) * mm, "end": v(-26.12, 70) * mm});
            skArc(sketch, "E195", {"start": v(76.88, 70) * mm, "mid": v(69.55, 87.68) * mm, "end": v(51.88, 95) * mm});
            skLineSegment(sketch, "E196", {"start": v(-1.12, 70) * mm, "end": v(51.88, 70) * mm, "construction": true});
            skLineSegment(sketch, "E197", {"start": v(76.88, 70) * mm, "end": v(76.88, 20) * mm});
            skLineSegment(sketch, "E198", {"start": v(-1.12, 95) * mm, "end": v(51.88, 95) * mm});
            skLineSegment(sketch, "E199.0", {"start": v(-32.12, 0) * mm, "end": v(48, 0) * mm, "construction": true});
            skLineSegment(sketch, "E200", {"start": v(76.88, 20) * mm, "end": v(-26.12, 20) * mm});
            skLineSegment(sketch, "E201", {"start": v(-26.12, 44) * mm, "end": v(76.88, 44) * mm});
            skLineSegment(sketch, "E202", {"start": v(-32.12, 0) * mm, "end": v(-26.12, 0) * mm, "construction": true});
            skLineSegment(sketch, "E203", {"start": v(-26.12, 44) * mm, "end": v(-26.12, 0) * mm});
            skLineSegment(sketch, "E204", {"start": v(-26.12, 44) * mm, "end": v(-26.12, 70) * mm});
            skLineSegment(sketch, "E205", {"start": v(48, 0) * mm, "end": v(48, 20) * mm, "construction": true});
            skCircle(sketch, "E206", {"center": v(-1.12, 70) * mm, "radius": 24 * mm});
            skCircle(sketch, "E207", {"center": v(51.88, 70) * mm, "radius": 24 * mm});
            skLineSegment(sketch, "E208", {"start": v(-1.12, 70) * mm, "end": v(-1.12, 20) * mm, "construction": true});
            skLineSegment(sketch, "E209", {"start": v(-1.12, 20) * mm, "end": v(51.88, 20) * mm, "construction": true});
            skLineSegment(sketch, "E210", {"start": v(51.88, 20) * mm, "end": v(51.88, 70) * mm, "construction": true});
            skPoint(sketch, "E211", {"position": v(51.88, 44) * mm});
            skPoint(sketch, "E212", {"position": v(-1.12, 44) * mm});
            skPoint(sketch, "E213", {"position": v(51.88, 32) * mm});
            skLineSegment(sketch, "E214", {"start": v(51.88, 32) * mm, "end": v(-1.12, 32) * mm, "construction": true});
            skCircle(sketch, "E215", {"center": v(-1.12, 32) * mm, "radius": 3 * mm});
            skCircle(sketch, "E216", {"center": v(51.88, 32) * mm, "radius": 3 * mm});
            skLineSegment(sketch, "E217", {"start": v(74.88, 44) * mm, "end": v(74.88, 20) * mm});
            skLineSegment(sketch, "E218", {"start": v(-24.12, 44) * mm, "end": v(-24.12, 20) * mm});
            skCircle(sketch, "E219", {"center": v(51.88, 70) * mm, "radius": 3 * mm});
            skCircle(sketch, "E220", {"center": v(-1.12, 70) * mm, "radius": 3 * mm});
            skCircle(sketch, "E221", {"center": v(-1.12, 70) * mm, "radius": 11 * mm});
            skCircle(sketch, "E222", {"center": v(51.88, 70) * mm, "radius": 11 * mm});
            skCircle(sketch, "E223", {"center": v(-1.12, 70) * mm, "radius": 4 * mm});
            skCircle(sketch, "E224", {"center": v(51.88, 70) * mm, "radius": 4 * mm});
            skCircle(sketch, "E225", {"center": v(-1.12, 70) * mm, "radius": 10 * mm});
            skCircle(sketch, "E226", {"center": v(51.88, 70) * mm, "radius": 10 * mm});
            skSolve(sketch);
        }
        {
            var Q0;
            {var subQ1=sQuery(id+"F35.wireOp",EDGE,"E200");Q0=makeQuery(id+"F35.imprint","IMPRINT",FACE,{"disambiguationData":[TD([[makeQuery(id+"F35.imprint","IMPRINT",EDGE,{"derivedFrom":subQ1}),-1.0]])]});}
            var Q1;
            Q1=makeQuery(id+"F35.imprint","IMPRINT",FACE,{"disambiguationData":[TD([[makeQuery(id+"F35.imprint","IMPRINT",EDGE,{"derivedFrom":sQuery(id+"F35.wireOp",EDGE,"E194")}),1.0]])]});
            var Q2;
            Q2=makeQuery(id+"F35.imprint","IMPRINT",FACE,{"disambiguationData":[TD([[makeQuery(id+"F35.imprint","IMPRINT",EDGE,{"derivedFrom":sQuery(id+"F35.wireOp",EDGE,"E206")}),1.0]])]});
            var Q3;
            Q3=makeQuery(id+"F35.imprint","IMPRINT",FACE,{"disambiguationData":[TD([[makeQuery(id+"F35.imprint","IMPRINT",EDGE,{"derivedFrom":sQuery(id+"F35.wireOp",EDGE,"E207")}),1.0]])]});
            var Q4;
            Q4=makeQuery(id+"F35.imprint","IMPRINT",FACE,{"disambiguationData":[TD([[makeQuery(id+"F35.imprint","IMPRINT",EDGE,{"derivedFrom":sQuery(id+"F35.wireOp",EDGE,"E221")}),1.0]])]});
            var Q5;
            Q5=makeQuery(id+"F35.imprint","IMPRINT",FACE,{"disambiguationData":[TD([[makeQuery(id+"F35.imprint","IMPRINT",EDGE,{"derivedFrom":sQuery(id+"F35.wireOp",EDGE,"E220")}),-1.0]])]});
            var Q6;
            Q6=makeQuery(id+"F35.imprint","IMPRINT",FACE,{"disambiguationData":[TD([[makeQuery(id+"F35.imprint","IMPRINT",EDGE,{"derivedFrom":sQuery(id+"F35.wireOp",EDGE,"E222")}),1.0]])]});
            var Q7;
            Q7=makeQuery(id+"F35.imprint","IMPRINT",FACE,{"disambiguationData":[TD([[makeQuery(id+"F35.imprint","IMPRINT",EDGE,{"derivedFrom":sQuery(id+"F35.wireOp",EDGE,"E219")}),-1.0]])]});
            var Q8;
            Q8=makeQuery(id+"F35.imprint","IMPRINT",FACE,{"disambiguationData":[TD([[makeQuery(id+"F35.imprint","IMPRINT",EDGE,{"derivedFrom":sQuery(id+"F35.wireOp",EDGE,"E215")}),-1.0]])]});
            var Q9;
            Q9=makeQuery(id+"F35.imprint","IMPRINT",FACE,{"disambiguationData":[TD([[makeQuery(id+"F35.imprint","IMPRINT",EDGE,{"derivedFrom":sQuery(id+"F35.wireOp",EDGE,"E223")}),-1.0]])]});
            var Q10;
            Q10=makeQuery(id+"F35.imprint","IMPRINT",FACE,{"disambiguationData":[TD([[makeQuery(id+"F35.imprint","IMPRINT",EDGE,{"derivedFrom":sQuery(id+"F35.wireOp",EDGE,"E224")}),-1.0]])]});
            extrude(context, id + "F36", {"entities" : qUnion([Q0, Q1, Q2, Q3, Q4, Q5, Q6, Q7, Q8, Q9, Q10]), "endBound" : BoundingType.SYMMETRIC, "depth" : 36 * mm});
        }
        {
            var Q0;
            Q0=makeQuery(id+"F35.imprint","IMPRINT",FACE,{"disambiguationData":[TD([[makeQuery(id+"F35.imprint","IMPRINT",EDGE,{"derivedFrom":sQuery(id+"F35.wireOp",EDGE,"E207")}),1.0]])]});
            var Q1;
            Q1=makeQuery(id+"F35.imprint","IMPRINT",FACE,{"disambiguationData":[TD([[makeQuery(id+"F35.imprint","IMPRINT",EDGE,{"derivedFrom":sQuery(id+"F35.wireOp",EDGE,"E206")}),1.0]])]});
            var Q2;
            Q2=makeQuery(id+"F35.imprint","IMPRINT",FACE,{"disambiguationData":[TD([[makeQuery(id+"F35.imprint","IMPRINT",EDGE,{"derivedFrom":sQuery(id+"F35.wireOp",EDGE,"E194")}),1.0]])]});
            var Q3;
            {var subQ1=sQuery(id+"F35.wireOp",EDGE,"E200");Q3=makeQuery(id+"F35.imprint","IMPRINT",FACE,{"disambiguationData":[TD([[makeQuery(id+"F35.imprint","IMPRINT",EDGE,{"derivedFrom":subQ1}),-1.0]])]});}
            var Q4;
            Q4=makeQuery(id+"F35.imprint","IMPRINT",FACE,{"disambiguationData":[TD([[makeQuery(id+"F35.imprint","IMPRINT",EDGE,{"derivedFrom":sQuery(id+"F35.wireOp",EDGE,"E223")}),-1.0]])]});
            var Q5;
            Q5=makeQuery(id+"F35.imprint","IMPRINT",FACE,{"disambiguationData":[TD([[makeQuery(id+"F35.imprint","IMPRINT",EDGE,{"derivedFrom":sQuery(id+"F35.wireOp",EDGE,"E224")}),-1.0]])]});
            var Q6;
            Q6=makeQuery(id+"F35.imprint","IMPRINT",FACE,{"disambiguationData":[TD([[makeQuery(id+"F35.imprint","IMPRINT",EDGE,{"derivedFrom":sQuery(id+"F35.wireOp",EDGE,"E222")}),1.0]])]});
            var Q7;
            Q7=makeQuery(id+"F35.imprint","IMPRINT",FACE,{"disambiguationData":[TD([[makeQuery(id+"F35.imprint","IMPRINT",EDGE,{"derivedFrom":sQuery(id+"F35.wireOp",EDGE,"E221")}),1.0]])]});
            var Q8;
            Q8=makeQuery(id+"F35.imprint","IMPRINT",FACE,{"disambiguationData":[TD([[makeQuery(id+"F35.imprint","IMPRINT",EDGE,{"derivedFrom":sQuery(id+"F35.wireOp",EDGE,"E220")}),-1.0]])]});
            var Q9;
            Q9=makeQuery(id+"F35.imprint","IMPRINT",FACE,{"disambiguationData":[TD([[makeQuery(id+"F35.imprint","IMPRINT",EDGE,{"derivedFrom":sQuery(id+"F35.wireOp",EDGE,"E219")}),-1.0]])]});
            var Q10;
            Q10=makeQuery(id+"F35.imprint","IMPRINT",FACE,{"disambiguationData":[TD([[makeQuery(id+"F35.imprint","IMPRINT",EDGE,{"derivedFrom":sQuery(id+"F35.wireOp",EDGE,"E215")}),-1.0]])]});
            extrude(context, id + "F37", {"entities" : qUnion([Q0, Q1, Q2, Q3, Q4, Q5, Q6, Q7, Q8, Q9, Q10]), "endBound" : BoundingType.SYMMETRIC, "depth" : 24 * mm});
        }
        {
            var Q0;
            Q0=makeQuery(id+"F35.imprint","IMPRINT",FACE,{"disambiguationData":[TD([[makeQuery(id+"F35.imprint","IMPRINT",EDGE,{"derivedFrom":sQuery(id+"F35.wireOp",EDGE,"E215")}),-1.0]])]});
            extrude(context, id + "F38", {"entities" : qUnion([Q0]), "endBound" : BoundingType.SYMMETRIC, "depth" : 24 * mm});
        }
        {
            var Q0;
            Q0=makeQuery(id+"F35.imprint","IMPRINT",FACE,{"disambiguationData":[TD([[makeQuery(id+"F35.imprint","IMPRINT",EDGE,{"derivedFrom":sQuery(id+"F35.wireOp",EDGE,"E207")}),1.0]])]});
            var Q1;
            Q1=makeQuery(id+"F35.imprint","IMPRINT",FACE,{"disambiguationData":[TD([[makeQuery(id+"F35.imprint","IMPRINT",EDGE,{"derivedFrom":sQuery(id+"F35.wireOp",EDGE,"E206")}),1.0]])]});
            extrude(context, id + "F39", {"entities" : qUnion([Q0, Q1]), "endBound" : BoundingType.SYMMETRIC, "depth" : 23 * mm});
        }
        {
            var Q0;
            Q0=makeQuery(id+"F35.imprint","IMPRINT",FACE,{"disambiguationData":[TD([[makeQuery(id+"F35.imprint","IMPRINT",EDGE,{"derivedFrom":sQuery(id+"F35.wireOp",EDGE,"E221")}),1.0]])]});
            var Q1;
            Q1=makeQuery(id+"F35.imprint","IMPRINT",FACE,{"disambiguationData":[TD([[makeQuery(id+"F35.imprint","IMPRINT",EDGE,{"derivedFrom":sQuery(id+"F35.wireOp",EDGE,"E222")}),1.0]])]});
            extrude(context, id + "F40", {"entities" : qUnion([Q0, Q1]), "endBound" : BoundingType.SYMMETRIC, "depth" : 11 * mm});
        }
        {
            var Q0;
            Q0=makeQuery(id+"F37.opExtrude","SWEPT_BODY",BODY,{"disambiguationData":[OSD([sQuery(id+"F35.wireOp",EDGE,"E194"),sQuery(id+"F35.wireOp",EDGE,"E195"),sQuery(id+"F35.wireOp",EDGE,"E197"),sQuery(id+"F35.wireOp",EDGE,"E198"),sQuery(id+"F35.wireOp",EDGE,"E200"),sQuery(id+"F35.wireOp",EDGE,"E203"),sQuery(id+"F35.wireOp",EDGE,"E204"),sQuery(id+"F35.wireOp",EDGE,"E215"),sQuery(id+"F35.wireOp",EDGE,"E216"),sQuery(id+"F35.wireOp",EDGE,"E219"),sQuery(id+"F35.wireOp",EDGE,"E220")])]});
            var Q1;
            Q1=makeQuery(id+"F36.opExtrude","SWEPT_BODY",BODY,{"disambiguationData":[OSD([sQuery(id+"F35.wireOp",EDGE,"E194"),sQuery(id+"F35.wireOp",EDGE,"E195"),sQuery(id+"F35.wireOp",EDGE,"E197"),sQuery(id+"F35.wireOp",EDGE,"E198"),sQuery(id+"F35.wireOp",EDGE,"E200"),sQuery(id+"F35.wireOp",EDGE,"E203"),sQuery(id+"F35.wireOp",EDGE,"E204"),sQuery(id+"F35.wireOp",EDGE,"E215"),sQuery(id+"F35.wireOp",EDGE,"E216"),sQuery(id+"F35.wireOp",EDGE,"E219"),sQuery(id+"F35.wireOp",EDGE,"E220")])]});
            booleanBodies(context, id + "F41", {"operationType" : BooleanOperationType.SUBTRACTION, "tools" : qUnion([Q0]), "targets" : qUnion([Q1])});
        }
    });
